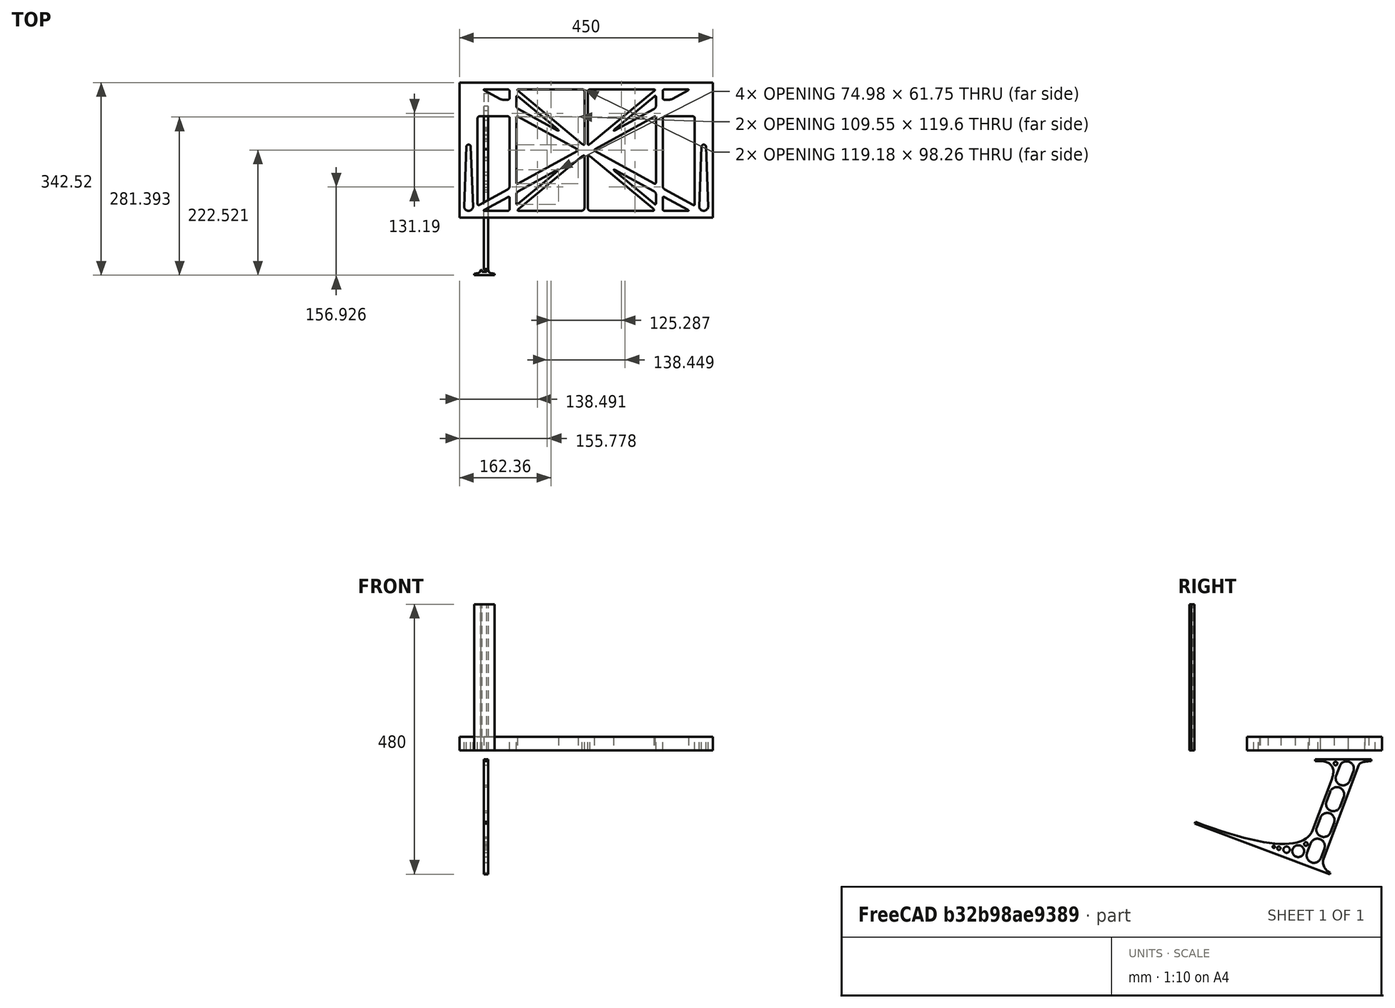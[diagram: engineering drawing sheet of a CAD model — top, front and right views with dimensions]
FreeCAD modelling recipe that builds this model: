
FCSTD DOCUMENT  (FreeCAD 0.19R0.19.2)
Label: laptopStand170FCStd
License: All rights reserved
LicenseURL: http://en.wikipedia.org/wiki/All_rights_reserved
objects: Sketcher::SketchObject×4, Part::Extrusion×3
note: 7 computed .brp shape members not serialized (recipe doc carries the construction recipe); baked Part::Feature solids carry a one-line shape summary decoded from their .brp

FEATURE [Sketcher::SketchObject] Sketch
  FullyConstrained = false
  sketch-geometry (349):
    g0: LineSegment StartX=-10.9272 StartY=-82.7794 StartZ=0 EndX=46.0728 EndY=-51.4823 EndZ=0
    g1: LineSegment StartX=-10.9272 StartY=76.4095 StartZ=0 EndX=-10.9272 EndY=-82.7794 EndZ=0
    g2: LineSegment StartX=46.0728 StartY=76.4095 StartZ=0 EndX=46.0728 EndY=-51.4823 EndZ=0
    g3: LineSegment StartX=-42.9272 StartY=136.221 StartZ=0 EndX=-42.9272 EndY=-103.779 EndZ=0
    g4: LineSegment StartX=407.073 StartY=136.221 StartZ=0 EndX=407.073 EndY=-103.779 EndZ=0
    g5: ArcOfCircle CenterX=-26.9272 CenterY=-83.7794 CenterZ=0 NormalX=0 NormalY=0 NormalZ=1 AngleXU=0 Radius=8 StartAngle=3.14159 EndAngle=6.28319
    g6: ArcOfCircle CenterX=391.073 CenterY=22.1087 CenterZ=0 NormalX=0 NormalY=0 NormalZ=1 AngleXU=0 Radius=8 StartAngle=-4.4e-15 EndAngle=3.14159
    g7: LineSegment StartX=399.073 StartY=22.1087 StartZ=0 EndX=399.073 EndY=-83.7794 EndZ=0
    g8: LineSegment StartX=383.073 StartY=22.1087 StartZ=0 EndX=383.073 EndY=-83.7794 EndZ=0
    g9: ArcOfCircle CenterX=391.073 CenterY=-83.7794 CenterZ=0 NormalX=0 NormalY=0 NormalZ=1 AngleXU=0 Radius=8 StartAngle=3.14159 EndAngle=6.28319
    g10: Circle CenterX=175.022 CenterY=27.0628 CenterZ=0 NormalX=0 NormalY=0 NormalZ=1 AngleXU=0 Radius=1
    g11: Circle CenterX=179.022 CenterY=24.8665 CenterZ=0 NormalX=0 NormalY=0 NormalZ=1 AngleXU=0 Radius=1
    g12: Circle CenterX=179.022 CenterY=27.0628 CenterZ=0 NormalX=0 NormalY=0 NormalZ=1 AngleXU=0 Radius=1
    g13: BSplineCurve PolesCount=3 KnotsCount=2 Degree=2 IsPeriodic=0
    g14: GeomPoint X=175.022 Y=27.0628 Z=0
    g15: GeomPoint X=179.022 Y=27.0628 Z=0
    g16: Circle CenterX=189.124 CenterY=27.0628 CenterZ=0 NormalX=0 NormalY=0 NormalZ=1 AngleXU=0 Radius=1
    g17: Circle CenterX=185.124 CenterY=24.8665 CenterZ=0 NormalX=0 NormalY=0 NormalZ=1 AngleXU=0 Radius=1
    g18: Circle CenterX=185.124 CenterY=27.0628 CenterZ=0 NormalX=0 NormalY=0 NormalZ=1 AngleXU=0 Radius=1
    g19: BSplineCurve PolesCount=3 KnotsCount=2 Degree=2 IsPeriodic=0
    g20: GeomPoint X=189.124 Y=27.0628 Z=0
    g21: GeomPoint X=185.124 Y=27.0628 Z=0
    g22: Circle CenterX=175.022 CenterY=5.37834 CenterZ=0 NormalX=0 NormalY=0 NormalZ=1 AngleXU=0 Radius=1
    g23: Circle CenterX=179.022 CenterY=7.57463 CenterZ=0 NormalX=0 NormalY=0 NormalZ=1 AngleXU=0 Radius=1
    g24: Circle CenterX=179.022 CenterY=5.34704 CenterZ=0 NormalX=0 NormalY=0 NormalZ=1 AngleXU=0 Radius=1
    g25: BSplineCurve PolesCount=3 KnotsCount=2 Degree=2 IsPeriodic=0
    g26: GeomPoint X=175.022 Y=5.37834 Z=0
    g27: GeomPoint X=179.022 Y=5.34704 Z=0
    g28: Circle CenterX=189.124 CenterY=5.37834 CenterZ=0 NormalX=0 NormalY=0 NormalZ=1 AngleXU=0 Radius=1
    g29: Circle CenterX=185.124 CenterY=7.57463 CenterZ=0 NormalX=0 NormalY=0 NormalZ=1 AngleXU=0 Radius=1
    g30: Circle CenterX=185.124 CenterY=5.34704 CenterZ=0 NormalX=0 NormalY=0 NormalZ=1 AngleXU=0 Radius=1
    g31: BSplineCurve PolesCount=3 KnotsCount=2 Degree=2 IsPeriodic=0
    g32: GeomPoint X=189.124 Y=5.37834 Z=0
    g33: GeomPoint X=185.124 Y=5.34704 Z=0
    g34: Circle CenterX=165.871 CenterY=18.1458 CenterZ=0 NormalX=0 NormalY=0 NormalZ=1 AngleXU=0 Radius=1
    g35: Circle CenterX=169.377 CenterY=16.2206 CenterZ=0 NormalX=0 NormalY=0 NormalZ=1 AngleXU=0 Radius=1
    g36: Circle CenterX=165.871 CenterY=14.2954 CenterZ=0 NormalX=0 NormalY=0 NormalZ=1 AngleXU=0 Radius=1
    g37: BSplineCurve PolesCount=3 KnotsCount=2 Degree=2 IsPeriodic=0
    g38: GeomPoint X=165.871 Y=18.1458 Z=0
    g39: GeomPoint X=165.871 Y=14.2954 Z=0
    g40: Circle CenterX=198.275 CenterY=18.1458 CenterZ=0 NormalX=0 NormalY=0 NormalZ=1 AngleXU=0 Radius=1
    g41: Circle CenterX=194.768 CenterY=16.2206 CenterZ=0 NormalX=0 NormalY=0 NormalZ=1 AngleXU=0 Radius=1
    g42: Circle CenterX=198.275 CenterY=14.2954 CenterZ=0 NormalX=0 NormalY=0 NormalZ=1 AngleXU=0 Radius=1
    g43: BSplineCurve PolesCount=3 KnotsCount=2 Degree=2 IsPeriodic=0
    g44: GeomPoint X=198.275 Y=18.1458 Z=0
    g45: GeomPoint X=198.275 Y=14.2954 Z=0
    g46: LineSegment StartX=407.073 StartY=-103.779 StartZ=0 EndX=-42.9272 EndY=-103.779 EndZ=0
    g47: LineSegment StartX=407.073 StartY=136.221 StartZ=0 EndX=-42.9272 EndY=136.221 EndZ=0
    g48: LineSegment StartX=46.0728 StartY=76.4095 StartZ=0 EndX=-10.9272 EndY=76.4095 EndZ=0
    g49: Circle CenterX=125.607 CenterY=54.1951 CenterZ=0 NormalX=0 NormalY=0 NormalZ=1 AngleXU=0 Radius=1
    g50: Circle CenterX=139.632 CenterY=46.4944 CenterZ=0 NormalX=0 NormalY=0 NormalZ=1 AngleXU=0 Radius=1
    g51: Circle CenterX=127.326 CenterY=56.7187 CenterZ=0 NormalX=0 NormalY=0 NormalZ=1 AngleXU=0 Radius=1
    g52: BSplineCurve PolesCount=3 KnotsCount=2 Degree=2 IsPeriodic=0
    g53: GeomPoint X=125.607 Y=54.1951 Z=0
    g54: GeomPoint X=127.326 Y=56.7187 Z=0
    g55: Circle CenterX=236.821 CenterY=56.7187 CenterZ=0 NormalX=0 NormalY=0 NormalZ=1 AngleXU=0 Radius=1
    g56: Circle CenterX=224.513 CenterY=46.4944 CenterZ=0 NormalX=0 NormalY=0 NormalZ=1 AngleXU=0 Radius=1
    g57: Circle CenterX=238.538 CenterY=54.1951 CenterZ=0 NormalX=0 NormalY=0 NormalZ=1 AngleXU=0 Radius=1
    g58: BSplineCurve PolesCount=3 KnotsCount=2 Degree=2 IsPeriodic=0
    g59: GeomPoint X=236.821 Y=56.7187 Z=0
    g60: GeomPoint X=238.538 Y=54.1951 Z=0
    g61: Circle CenterX=238.538 CenterY=-21.7539 CenterZ=0 NormalX=0 NormalY=0 NormalZ=1 AngleXU=0 Radius=1
    g62: Circle CenterX=224.513 CenterY=-14.0532 CenterZ=0 NormalX=0 NormalY=0 NormalZ=1 AngleXU=0 Radius=1
    g63: Circle CenterX=236.821 CenterY=-24.2775 CenterZ=0 NormalX=0 NormalY=0 NormalZ=1 AngleXU=0 Radius=1
    g64: BSplineCurve PolesCount=3 KnotsCount=2 Degree=2 IsPeriodic=0
    g65: GeomPoint X=238.538 Y=-21.7539 Z=0
    g66: GeomPoint X=236.821 Y=-24.2775 Z=0
    g67: Circle CenterX=125.607 CenterY=-21.7539 CenterZ=0 NormalX=0 NormalY=0 NormalZ=1 AngleXU=0 Radius=1
    g68: Circle CenterX=139.632 CenterY=-14.0532 CenterZ=0 NormalX=0 NormalY=0 NormalZ=1 AngleXU=0 Radius=1
    g69: Circle CenterX=127.325 CenterY=-24.2775 CenterZ=0 NormalX=0 NormalY=0 NormalZ=1 AngleXU=0 Radius=1
    g70: BSplineCurve PolesCount=3 KnotsCount=2 Degree=2 IsPeriodic=0
    g71: GeomPoint X=125.607 Y=-21.7539 Z=0
    g72: GeomPoint X=127.325 Y=-24.2775 Z=0
    g73: Circle CenterX=302.996 CenterY=111.695 CenterZ=0 NormalX=0 NormalY=0 NormalZ=1 AngleXU=0 Radius=1
    g74: Circle CenterX=306.073 CenterY=114.251 CenterZ=0 NormalX=0 NormalY=0 NormalZ=1 AngleXU=0 Radius=1
    g75: Circle CenterX=306.073 CenterY=110.251 CenterZ=0 NormalX=0 NormalY=0 NormalZ=1 AngleXU=0 Radius=1
    g76: BSplineCurve PolesCount=3 KnotsCount=2 Degree=2 IsPeriodic=0
    g77: GeomPoint X=302.996 Y=111.695 Z=0
    g78: GeomPoint X=306.073 Y=110.251 Z=0
    g79: Circle CenterX=306.073 CenterY=95.2763 CenterZ=0 NormalX=0 NormalY=0 NormalZ=1 AngleXU=0 Radius=1
    g80: Circle CenterX=306.073 CenterY=91.2763 CenterZ=0 NormalX=0 NormalY=0 NormalZ=1 AngleXU=0 Radius=1
    g81: Circle CenterX=302.567 CenterY=89.3511 CenterZ=0 NormalX=0 NormalY=0 NormalZ=1 AngleXU=0 Radius=1
    g82: BSplineCurve PolesCount=3 KnotsCount=2 Degree=2 IsPeriodic=0
    g83: GeomPoint X=306.073 Y=95.2763 Z=0
    g84: GeomPoint X=302.567 Y=89.3511 Z=0
    g85: LineSegment StartX=306.073 StartY=110.251 StartZ=0 EndX=306.073 EndY=95.2763 EndZ=0
    g86: LineSegment StartX=302.996 StartY=111.695 StartZ=0 EndX=236.821 EndY=56.7187 EndZ=0
    g87: LineSegment StartX=238.538 StartY=54.1951 StartZ=0 EndX=302.567 EndY=89.3511 EndZ=0
    g88: Circle CenterX=61.1496 CenterY=111.695 CenterZ=0 NormalX=0 NormalY=0 NormalZ=1 AngleXU=0 Radius=1
    g89: Circle CenterX=58.0728 CenterY=114.251 CenterZ=0 NormalX=0 NormalY=0 NormalZ=1 AngleXU=0 Radius=1
    g90: Circle CenterX=58.0728 CenterY=110.251 CenterZ=0 NormalX=0 NormalY=0 NormalZ=1 AngleXU=0 Radius=1
    g91: BSplineCurve PolesCount=3 KnotsCount=2 Degree=2 IsPeriodic=0
    g92: GeomPoint X=61.1496 Y=111.695 Z=0
    g93: GeomPoint X=58.0728 Y=110.251 Z=0
    g94: Circle CenterX=61.5791 CenterY=89.3511 CenterZ=0 NormalX=0 NormalY=0 NormalZ=1 AngleXU=0 Radius=1
    g95: Circle CenterX=58.0728 CenterY=91.2763 CenterZ=0 NormalX=0 NormalY=0 NormalZ=1 AngleXU=0 Radius=1
    g96: Circle CenterX=58.0728 CenterY=95.2763 CenterZ=0 NormalX=0 NormalY=0 NormalZ=1 AngleXU=0 Radius=1
    g97: BSplineCurve PolesCount=3 KnotsCount=2 Degree=2 IsPeriodic=0
    g98: GeomPoint X=61.5791 Y=89.3511 Z=0
    g99: GeomPoint X=58.0728 Y=95.2763 Z=0
    g100: LineSegment StartX=58.0728 StartY=110.251 StartZ=0 EndX=58.0728 EndY=95.2763 EndZ=0
    g101: LineSegment StartX=61.1496 StartY=111.695 StartZ=0 EndX=127.326 EndY=56.7187 EndZ=0
    g102: LineSegment StartX=125.607 StartY=54.1951 StartZ=0 EndX=61.5791 EndY=89.3511 EndZ=0
    g103: Circle CenterX=61.5791 CenterY=-56.9099 CenterZ=0 NormalX=0 NormalY=0 NormalZ=1 AngleXU=0 Radius=1
    g104: Circle CenterX=58.0728 CenterY=-58.8351 CenterZ=0 NormalX=0 NormalY=0 NormalZ=1 AngleXU=0 Radius=1
    g105: Circle CenterX=58.0728 CenterY=-62.8351 CenterZ=0 NormalX=0 NormalY=0 NormalZ=1 AngleXU=0 Radius=1
    g106: BSplineCurve PolesCount=3 KnotsCount=2 Degree=2 IsPeriodic=0
    g107: GeomPoint X=61.5791 Y=-56.9099 Z=0
    g108: GeomPoint X=58.0728 Y=-62.8351 Z=0
    g109: Circle CenterX=58.0728 CenterY=-77.8102 CenterZ=0 NormalX=0 NormalY=0 NormalZ=1 AngleXU=0 Radius=1
    g110: Circle CenterX=58.0728 CenterY=-81.8102 CenterZ=0 NormalX=0 NormalY=0 NormalZ=1 AngleXU=0 Radius=1
    g111: Circle CenterX=61.1496 CenterY=-79.2541 CenterZ=0 NormalX=0 NormalY=0 NormalZ=1 AngleXU=0 Radius=1
    g112: BSplineCurve PolesCount=3 KnotsCount=2 Degree=2 IsPeriodic=0
    g113: GeomPoint X=58.0728 Y=-77.8102 Z=0
    g114: GeomPoint X=61.1496 Y=-79.2541 Z=0
    g115: LineSegment StartX=58.0728 StartY=-62.8351 StartZ=0 EndX=58.0728 EndY=-77.8102 EndZ=0
    g116: LineSegment StartX=61.1496 StartY=-79.2541 StartZ=0 EndX=127.325 EndY=-24.2775 EndZ=0
    g117: LineSegment StartX=125.607 StartY=-21.7539 StartZ=0 EndX=61.5791 EndY=-56.9099 EndZ=0
    g118: Circle CenterX=302.567 CenterY=-56.9099 CenterZ=0 NormalX=0 NormalY=0 NormalZ=1 AngleXU=0 Radius=1
    g119: Circle CenterX=306.073 CenterY=-58.8351 CenterZ=0 NormalX=0 NormalY=0 NormalZ=1 AngleXU=0 Radius=1
    g120: Circle CenterX=306.073 CenterY=-62.8351 CenterZ=0 NormalX=0 NormalY=0 NormalZ=1 AngleXU=0 Radius=1
    g121: BSplineCurve PolesCount=3 KnotsCount=2 Degree=2 IsPeriodic=0
    g122: GeomPoint X=302.567 Y=-56.9099 Z=0
    g123: GeomPoint X=306.073 Y=-62.8351 Z=0
    g124: Circle CenterX=302.996 CenterY=-79.2541 CenterZ=0 NormalX=0 NormalY=0 NormalZ=1 AngleXU=0 Radius=1
    g125: Circle CenterX=306.073 CenterY=-81.8102 CenterZ=0 NormalX=0 NormalY=0 NormalZ=1 AngleXU=0 Radius=1
    g126: Circle CenterX=306.073 CenterY=-77.8102 CenterZ=0 NormalX=0 NormalY=0 NormalZ=1 AngleXU=0 Radius=1
    g127: BSplineCurve PolesCount=3 KnotsCount=2 Degree=2 IsPeriodic=0
    g128: GeomPoint X=302.996 Y=-79.2541 Z=0
    g129: GeomPoint X=306.073 Y=-77.8102 Z=0
    g130: LineSegment StartX=306.073 StartY=-62.8351 StartZ=0 EndX=306.073 EndY=-77.8102 EndZ=0
    g131: LineSegment StartX=302.996 StartY=-79.2541 StartZ=0 EndX=236.821 EndY=-24.2775 EndZ=0
    g132: LineSegment StartX=238.538 StartY=-21.7539 StartZ=0 EndX=302.567 EndY=-56.9099 EndZ=0
    g133: Circle CenterX=61.6457 CenterY=-88.8112 CenterZ=0 NormalX=0 NormalY=0 NormalZ=1 AngleXU=0 Radius=1
    g134: Circle CenterX=58.0728 CenterY=-91.7794 CenterZ=0 NormalX=0 NormalY=0 NormalZ=1 AngleXU=0 Radius=1
    g135: Circle CenterX=63.9135 CenterY=-91.7794 CenterZ=0 NormalX=0 NormalY=0 NormalZ=1 AngleXU=0 Radius=1
    g136: BSplineCurve PolesCount=3 KnotsCount=2 Degree=2 IsPeriodic=0
    g137: GeomPoint X=61.6457 Y=-88.8112 Z=0
    g138: GeomPoint X=63.9135 Y=-91.7794 Z=0
    g139: Circle CenterX=179.022 CenterY=-85.8163 CenterZ=0 NormalX=0 NormalY=0 NormalZ=1 AngleXU=0 Radius=1
    g140: Circle CenterX=179.022 CenterY=-91.7794 CenterZ=0 NormalX=0 NormalY=0 NormalZ=1 AngleXU=0 Radius=1
    g141: Circle CenterX=171.895 CenterY=-91.7794 CenterZ=0 NormalX=0 NormalY=0 NormalZ=1 AngleXU=0 Radius=1
    g142: BSplineCurve PolesCount=3 KnotsCount=2 Degree=2 IsPeriodic=0
    g143: GeomPoint X=179.022 Y=-85.8163 Z=0
    g144: GeomPoint X=171.895 Y=-91.7794 Z=0
    g145: Circle CenterX=185.124 CenterY=-86.2028 CenterZ=0 NormalX=0 NormalY=0 NormalZ=1 AngleXU=0 Radius=1
    g146: Circle CenterX=185.124 CenterY=-91.7794 CenterZ=0 NormalX=0 NormalY=0 NormalZ=1 AngleXU=0 Radius=1
    g147: Circle CenterX=191.747 CenterY=-91.7794 CenterZ=0 NormalX=0 NormalY=0 NormalZ=1 AngleXU=0 Radius=1
    g148: BSplineCurve PolesCount=3 KnotsCount=2 Degree=2 IsPeriodic=0
    g149: GeomPoint X=185.124 Y=-86.2028 Z=0
    g150: GeomPoint X=191.747 Y=-91.7794 Z=0
    g151: Circle CenterX=299.888 CenterY=-86.6413 CenterZ=0 NormalX=0 NormalY=0 NormalZ=1 AngleXU=0 Radius=1
    g152: Circle CenterX=306.073 CenterY=-91.7794 CenterZ=0 NormalX=0 NormalY=0 NormalZ=1 AngleXU=0 Radius=1
    g153: Circle CenterX=298.776 CenterY=-91.7794 CenterZ=0 NormalX=0 NormalY=0 NormalZ=1 AngleXU=0 Radius=1
    g154: BSplineCurve PolesCount=3 KnotsCount=2 Degree=2 IsPeriodic=0
    g155: GeomPoint X=299.888 Y=-86.6413 Z=0
    g156: GeomPoint X=298.776 Y=-91.7794 Z=0
    g157: LineSegment StartX=189.124 StartY=5.37834 StartZ=0 EndX=299.888 EndY=-86.6413 EndZ=0
    g158: LineSegment StartX=298.776 StartY=-91.7794 StartZ=0 EndX=191.747 EndY=-91.7794 EndZ=0
    g159: LineSegment StartX=185.124 StartY=-86.2028 StartZ=0 EndX=185.124 EndY=5.34704 EndZ=0
    g160: LineSegment StartX=179.022 StartY=5.34704 StartZ=0 EndX=179.022 EndY=-85.8163 EndZ=0
    g161: LineSegment StartX=171.895 StartY=-91.7794 StartZ=0 EndX=63.9135 EndY=-91.7794 EndZ=0
    g162: LineSegment StartX=61.6457 StartY=-88.8112 StartZ=0 EndX=175.022 EndY=5.37834 EndZ=0
    g163: Circle CenterX=302.073 CenterY=124.221 CenterZ=0 NormalX=0 NormalY=0 NormalZ=1 AngleXU=0 Radius=1
    g164: Circle CenterX=306.073 CenterY=124.221 CenterZ=0 NormalX=0 NormalY=0 NormalZ=1 AngleXU=0 Radius=1
    g165: Circle CenterX=302.996 CenterY=121.665 CenterZ=0 NormalX=0 NormalY=0 NormalZ=1 AngleXU=0 Radius=1
    g166: BSplineCurve PolesCount=3 KnotsCount=2 Degree=2 IsPeriodic=0
    g167: GeomPoint X=302.073 Y=124.221 Z=0
    g168: GeomPoint X=302.996 Y=121.665 Z=0
    g169: Circle CenterX=189.124 CenterY=124.221 CenterZ=0 NormalX=0 NormalY=0 NormalZ=1 AngleXU=0 Radius=1
    g170: Circle CenterX=185.124 CenterY=124.221 CenterZ=0 NormalX=0 NormalY=0 NormalZ=1 AngleXU=0 Radius=1
    g171: Circle CenterX=185.124 CenterY=120.221 CenterZ=0 NormalX=0 NormalY=0 NormalZ=1 AngleXU=0 Radius=1
    g172: BSplineCurve PolesCount=3 KnotsCount=2 Degree=2 IsPeriodic=0
    g173: GeomPoint X=189.124 Y=124.221 Z=0
    g174: GeomPoint X=185.124 Y=120.221 Z=0
    g175: Circle CenterX=175.022 CenterY=124.221 CenterZ=0 NormalX=0 NormalY=0 NormalZ=1 AngleXU=0 Radius=1
    g176: Circle CenterX=179.022 CenterY=124.221 CenterZ=0 NormalX=0 NormalY=0 NormalZ=1 AngleXU=0 Radius=1
    g177: Circle CenterX=179.022 CenterY=120.221 CenterZ=0 NormalX=0 NormalY=0 NormalZ=1 AngleXU=0 Radius=1
    g178: BSplineCurve PolesCount=3 KnotsCount=2 Degree=2 IsPeriodic=0
    g179: GeomPoint X=175.022 Y=124.221 Z=0
    g180: GeomPoint X=179.022 Y=120.221 Z=0
    g181: Circle CenterX=62.0728 CenterY=124.221 CenterZ=0 NormalX=0 NormalY=0 NormalZ=1 AngleXU=0 Radius=1
    g182: Circle CenterX=58.0728 CenterY=124.221 CenterZ=0 NormalX=0 NormalY=0 NormalZ=1 AngleXU=0 Radius=1
    g183: Circle CenterX=61.1496 CenterY=121.665 CenterZ=0 NormalX=0 NormalY=0 NormalZ=1 AngleXU=0 Radius=1
    g184: BSplineCurve PolesCount=3 KnotsCount=2 Degree=2 IsPeriodic=0
    g185: GeomPoint X=62.0728 Y=124.221 Z=0
    g186: GeomPoint X=61.1496 Y=121.665 Z=0
    g187: LineSegment StartX=62.0728 StartY=124.221 StartZ=0 EndX=175.022 EndY=124.221 EndZ=0
    g188: LineSegment StartX=179.022 StartY=120.221 StartZ=0 EndX=179.022 EndY=27.0628 EndZ=0
    g189: LineSegment StartX=185.124 StartY=27.0628 StartZ=0 EndX=185.124 EndY=120.221 EndZ=0
    g190: LineSegment StartX=189.124 StartY=124.221 StartZ=0 EndX=302.073 EndY=124.221 EndZ=0
    g191: LineSegment StartX=302.996 StartY=121.665 StartZ=0 EndX=189.124 EndY=27.0628 EndZ=0
    g192: LineSegment StartX=175.022 StartY=27.0628 StartZ=0 EndX=61.1496 EndY=121.665 EndZ=0
    g193: Circle CenterX=61.5791 CenterY=75.4095 CenterZ=0 NormalX=0 NormalY=0 NormalZ=1 AngleXU=0 Radius=1
    g194: Circle CenterX=58.0728 CenterY=77.3346 CenterZ=0 NormalX=0 NormalY=0 NormalZ=1 AngleXU=0 Radius=1
    g195: Circle CenterX=58.0728 CenterY=73.3346 CenterZ=0 NormalX=0 NormalY=0 NormalZ=1 AngleXU=0 Radius=1
    g196: BSplineCurve PolesCount=3 KnotsCount=2 Degree=2 IsPeriodic=0
    g197: GeomPoint X=61.5791 Y=75.4095 Z=0
    g198: GeomPoint X=58.0728 Y=73.3346 Z=0
    g199: Circle CenterX=58.0728 CenterY=-40.8935 CenterZ=0 NormalX=0 NormalY=0 NormalZ=1 AngleXU=0 Radius=1
    g200: Circle CenterX=58.0728 CenterY=-44.8935 CenterZ=0 NormalX=0 NormalY=0 NormalZ=1 AngleXU=0 Radius=1
    g201: Circle CenterX=61.5791 CenterY=-42.9683 CenterZ=0 NormalX=0 NormalY=0 NormalZ=1 AngleXU=0 Radius=1
    g202: BSplineCurve PolesCount=3 KnotsCount=2 Degree=2 IsPeriodic=0
    g203: GeomPoint X=58.0728 Y=-40.8935 Z=0
    g204: GeomPoint X=61.5791 Y=-42.9683 Z=0
    g205: LineSegment StartX=61.5791 StartY=-42.9683 StartZ=0 EndX=165.871 EndY=14.2954 EndZ=0
    g206: LineSegment StartX=165.871 StartY=18.1458 StartZ=0 EndX=61.5791 EndY=75.4095 EndZ=0
    g207: LineSegment StartX=58.0728 StartY=73.3346 StartZ=0 EndX=58.0728 EndY=-40.8935 EndZ=0
    g208: Circle CenterX=302.567 CenterY=-42.9683 CenterZ=0 NormalX=0 NormalY=0 NormalZ=1 AngleXU=0 Radius=1
    g209: Circle CenterX=306.073 CenterY=-44.8935 CenterZ=0 NormalX=0 NormalY=0 NormalZ=1 AngleXU=0 Radius=1
    g210: Circle CenterX=306.073 CenterY=-40.8935 CenterZ=0 NormalX=0 NormalY=0 NormalZ=1 AngleXU=0 Radius=1
    g211: BSplineCurve PolesCount=3 KnotsCount=2 Degree=2 IsPeriodic=0
    g212: GeomPoint X=302.567 Y=-42.9683 Z=0
    g213: GeomPoint X=306.073 Y=-40.8935 Z=0
    g214: Circle CenterX=306.073 CenterY=73.3346 CenterZ=0 NormalX=0 NormalY=0 NormalZ=1 AngleXU=0 Radius=1
    g215: Circle CenterX=306.073 CenterY=77.3346 CenterZ=0 NormalX=0 NormalY=0 NormalZ=1 AngleXU=0 Radius=1
    g216: Circle CenterX=302.567 CenterY=75.4095 CenterZ=0 NormalX=0 NormalY=0 NormalZ=1 AngleXU=0 Radius=1
    g217: BSplineCurve PolesCount=3 KnotsCount=2 Degree=2 IsPeriodic=0
    g218: GeomPoint X=306.073 Y=73.3346 Z=0
    g219: GeomPoint X=302.567 Y=75.4095 Z=0
    g220: LineSegment StartX=302.567 StartY=-42.9683 StartZ=0 EndX=198.275 EndY=14.2954 EndZ=0
    g221: LineSegment StartX=198.275 StartY=18.1458 StartZ=0 EndX=302.567 EndY=75.4095 EndZ=0
    g222: LineSegment StartX=306.073 StartY=73.3346 StartZ=0 EndX=306.073 EndY=-40.8935 EndZ=0
    g223: LineSegment StartX=322.073 StartY=105.865 StartZ=0 EndX=328.643 EndY=105.865 EndZ=0
    g224: LineSegment StartX=318.073 StartY=120.221 StartZ=0 EndX=318.073 EndY=109.865 EndZ=0
    g225: LineSegment StartX=336.157 StartY=107.779 StartZ=0 EndX=362.567 EndY=122.294 EndZ=0
    g226: Circle CenterX=362.073 CenterY=124.221 CenterZ=0 NormalX=0 NormalY=0 NormalZ=1 AngleXU=0 Radius=1
    g227: Circle CenterX=366.073 CenterY=124.221 CenterZ=0 NormalX=0 NormalY=0 NormalZ=1 AngleXU=0 Radius=1
    g228: Circle CenterX=362.567 CenterY=122.294 CenterZ=0 NormalX=0 NormalY=0 NormalZ=1 AngleXU=0 Radius=1
    g229: BSplineCurve PolesCount=3 KnotsCount=2 Degree=2 IsPeriodic=0
    g230: GeomPoint X=362.073 Y=124.221 Z=0
    g231: GeomPoint X=362.567 Y=122.294 Z=0
    g232: Circle CenterX=322.073 CenterY=124.221 CenterZ=0 NormalX=0 NormalY=0 NormalZ=1 AngleXU=0 Radius=1
    g233: Circle CenterX=318.073 CenterY=124.221 CenterZ=0 NormalX=0 NormalY=0 NormalZ=1 AngleXU=0 Radius=1
    g234: Circle CenterX=318.073 CenterY=120.221 CenterZ=0 NormalX=0 NormalY=0 NormalZ=1 AngleXU=0 Radius=1
    g235: BSplineCurve PolesCount=3 KnotsCount=2 Degree=2 IsPeriodic=0
    g236: GeomPoint X=322.073 Y=124.221 Z=0
    g237: GeomPoint X=318.073 Y=120.221 Z=0
    g238: Circle CenterX=322.073 CenterY=105.865 CenterZ=0 NormalX=0 NormalY=0 NormalZ=1 AngleXU=0 Radius=1
    g239: Circle CenterX=318.073 CenterY=105.865 CenterZ=0 NormalX=0 NormalY=0 NormalZ=1 AngleXU=0 Radius=1
    g240: Circle CenterX=318.073 CenterY=109.865 CenterZ=0 NormalX=0 NormalY=0 NormalZ=1 AngleXU=0 Radius=1
    g241: BSplineCurve PolesCount=3 KnotsCount=2 Degree=2 IsPeriodic=0
    g242: GeomPoint X=322.073 Y=105.865 Z=0
    g243: GeomPoint X=318.073 Y=109.865 Z=0
    g244: Circle CenterX=336.157 CenterY=107.779 CenterZ=0 NormalX=0 NormalY=0 NormalZ=1 AngleXU=0 Radius=1
    g245: Circle CenterX=332.651 CenterY=105.853 CenterZ=0 NormalX=0 NormalY=0 NormalZ=1 AngleXU=0 Radius=1
    g246: Circle CenterX=328.643 CenterY=105.865 CenterZ=0 NormalX=0 NormalY=0 NormalZ=1 AngleXU=0 Radius=1
    g247: BSplineCurve PolesCount=3 KnotsCount=2 Degree=2 IsPeriodic=0
    g248: GeomPoint X=336.157 Y=107.779 Z=0
    g249: GeomPoint X=328.643 Y=105.865 Z=0
    g250: LineSegment StartX=322.073 StartY=124.221 StartZ=0 EndX=362.073 EndY=124.221 EndZ=0
    g251: Circle CenterX=371.567 CenterY=-80.8644 CenterZ=0 NormalX=0 NormalY=0 NormalZ=1 AngleXU=0 Radius=1
    g252: Circle CenterX=375.073 CenterY=-82.7896 CenterZ=0 NormalX=0 NormalY=0 NormalZ=1 AngleXU=0 Radius=1
    g253: Circle CenterX=375.073 CenterY=-78.7896 CenterZ=0 NormalX=0 NormalY=0 NormalZ=1 AngleXU=0 Radius=1
    g254: BSplineCurve PolesCount=3 KnotsCount=2 Degree=2 IsPeriodic=0
    g255: GeomPoint X=371.567 Y=-80.8644 Z=0
    g256: GeomPoint X=375.073 Y=-78.7896 Z=0
    g257: Circle CenterX=321.579 CenterY=-53.4075 CenterZ=0 NormalX=0 NormalY=0 NormalZ=1 AngleXU=0 Radius=1
    g258: Circle CenterX=318.073 CenterY=-51.4823 CenterZ=0 NormalX=0 NormalY=0 NormalZ=1 AngleXU=0 Radius=1
    g259: Circle CenterX=318.073 CenterY=-47.4805 CenterZ=0 NormalX=0 NormalY=0 NormalZ=1 AngleXU=0 Radius=1
    g260: BSplineCurve PolesCount=3 KnotsCount=2 Degree=2 IsPeriodic=0
    g261: GeomPoint X=321.579 Y=-53.4075 Z=0
    g262: GeomPoint X=318.073 Y=-47.4805 Z=0
    g263: LineSegment StartX=371.567 StartY=-80.8644 StartZ=0 EndX=321.579 EndY=-53.4075 EndZ=0
    g264: Circle CenterX=321.579 CenterY=-67.3492 CenterZ=0 NormalX=0 NormalY=0 NormalZ=1 AngleXU=0 Radius=1
    g265: Circle CenterX=318.073 CenterY=-65.424 CenterZ=0 NormalX=0 NormalY=0 NormalZ=1 AngleXU=0 Radius=1
    g266: Circle CenterX=318.073 CenterY=-69.424 CenterZ=0 NormalX=0 NormalY=0 NormalZ=1 AngleXU=0 Radius=1
    g267: BSplineCurve PolesCount=3 KnotsCount=2 Degree=2 IsPeriodic=0
    g268: GeomPoint X=321.579 Y=-67.3492 Z=0
    g269: GeomPoint X=318.073 Y=-69.424 Z=0
    g270: Circle CenterX=362.567 CenterY=-89.8542 CenterZ=0 NormalX=0 NormalY=0 NormalZ=1 AngleXU=0 Radius=1
    g271: Circle CenterX=366.073 CenterY=-91.7794 CenterZ=0 NormalX=0 NormalY=0 NormalZ=1 AngleXU=0 Radius=1
    g272: Circle CenterX=362.073 CenterY=-91.7794 CenterZ=0 NormalX=0 NormalY=0 NormalZ=1 AngleXU=0 Radius=1
    g273: BSplineCurve PolesCount=3 KnotsCount=2 Degree=2 IsPeriodic=0
    g274: GeomPoint X=362.567 Y=-89.8542 Z=0
    g275: GeomPoint X=362.073 Y=-91.7794 Z=0
    g276: Circle CenterX=322.073 CenterY=-91.7794 CenterZ=0 NormalX=0 NormalY=0 NormalZ=1 AngleXU=0 Radius=1
    g277: Circle CenterX=318.073 CenterY=-91.7794 CenterZ=0 NormalX=0 NormalY=0 NormalZ=1 AngleXU=0 Radius=1
    g278: Circle CenterX=318.073 CenterY=-87.7794 CenterZ=0 NormalX=0 NormalY=0 NormalZ=1 AngleXU=0 Radius=1
    g279: BSplineCurve PolesCount=3 KnotsCount=2 Degree=2 IsPeriodic=0
    g280: GeomPoint X=322.073 Y=-91.7794 Z=0
    g281: GeomPoint X=318.073 Y=-87.7794 Z=0
    g282: LineSegment StartX=362.567 StartY=-89.8542 StartZ=0 EndX=321.579 EndY=-67.3492 EndZ=0
    g283: LineSegment StartX=318.073 StartY=-69.424 StartZ=0 EndX=318.073 EndY=-87.7794 EndZ=0
    g284: LineSegment StartX=322.073 StartY=-91.7794 StartZ=0 EndX=362.073 EndY=-91.7794 EndZ=0
    g285: Circle CenterX=2.07281 CenterY=124.221 CenterZ=0 NormalX=0 NormalY=0 NormalZ=1 AngleXU=0 Radius=1
    g286: Circle CenterX=1.57905 CenterY=122.295 CenterZ=0 NormalX=0 NormalY=0 NormalZ=1 AngleXU=0 Radius=1
    g287: BSplineCurve PolesCount=3 KnotsCount=2 Degree=2 IsPeriodic=0
    g288: GeomPoint X=2.07281 Y=124.221 Z=0
    g289: GeomPoint X=1.57905 Y=122.295 Z=0
    g290: Circle CenterX=42.0728 CenterY=124.221 CenterZ=0 NormalX=0 NormalY=0 NormalZ=1 AngleXU=0 Radius=1
    g291: Circle CenterX=46.0728 CenterY=124.221 CenterZ=0 NormalX=0 NormalY=0 NormalZ=1 AngleXU=0 Radius=1
    g292: Circle CenterX=46.0728 CenterY=120.221 CenterZ=0 NormalX=0 NormalY=0 NormalZ=1 AngleXU=0 Radius=1
    g293: BSplineCurve PolesCount=3 KnotsCount=2 Degree=2 IsPeriodic=0
    g294: GeomPoint X=42.0728 Y=124.221 Z=0
    g295: GeomPoint X=46.0728 Y=120.221 Z=0
    g296: Circle CenterX=46.0728 CenterY=109.865 CenterZ=0 NormalX=0 NormalY=0 NormalZ=1 AngleXU=0 Radius=1
    g297: Circle CenterX=46.0728 CenterY=105.865 CenterZ=0 NormalX=0 NormalY=0 NormalZ=1 AngleXU=0 Radius=1
    g298: Circle CenterX=42.0728 CenterY=105.865 CenterZ=0 NormalX=0 NormalY=0 NormalZ=1 AngleXU=0 Radius=1
    g299: BSplineCurve PolesCount=3 KnotsCount=2 Degree=2 IsPeriodic=0
    g300: GeomPoint X=46.0728 Y=109.865 Z=0
    g301: GeomPoint X=42.0728 Y=105.865 Z=0
    g302: Circle CenterX=35.5028 CenterY=105.865 CenterZ=0 NormalX=0 NormalY=0 NormalZ=1 AngleXU=0 Radius=1
    g303: Circle CenterX=31.5028 CenterY=105.865 CenterZ=0 NormalX=0 NormalY=0 NormalZ=1 AngleXU=0 Radius=1
    g304: Circle CenterX=27.9965 CenterY=107.79 CenterZ=0 NormalX=0 NormalY=0 NormalZ=1 AngleXU=0 Radius=1
    g305: BSplineCurve PolesCount=3 KnotsCount=2 Degree=2 IsPeriodic=0
    g306: GeomPoint X=35.5028 Y=105.865 Z=0
    g307: GeomPoint X=27.9965 Y=107.79 Z=0
    g308: LineSegment StartX=2.07281 StartY=124.221 StartZ=0 EndX=42.0728 EndY=124.221 EndZ=0
    g309: LineSegment StartX=46.0728 StartY=120.221 StartZ=0 EndX=46.0728 EndY=109.865 EndZ=0
    g310: LineSegment StartX=42.0728 StartY=105.865 StartZ=0 EndX=35.5028 EndY=105.865 EndZ=0
    g311: LineSegment StartX=27.9965 StartY=107.79 StartZ=0 EndX=1.57905 EndY=122.295 EndZ=0
    g312: Circle CenterX=42.5666 CenterY=-67.3492 CenterZ=0 NormalX=0 NormalY=0 NormalZ=1 AngleXU=0 Radius=1
    g313: Circle CenterX=46.0728 CenterY=-65.424 CenterZ=0 NormalX=0 NormalY=0 NormalZ=1 AngleXU=0 Radius=1
    g314: Circle CenterX=46.0728 CenterY=-69.424 CenterZ=0 NormalX=0 NormalY=0 NormalZ=1 AngleXU=0 Radius=1
    g315: BSplineCurve PolesCount=3 KnotsCount=2 Degree=2 IsPeriodic=0
    g316: GeomPoint X=42.5666 Y=-67.3492 Z=0
    g317: GeomPoint X=46.0728 Y=-69.424 Z=0
    g318: Circle CenterX=46.0728 CenterY=-87.7794 CenterZ=0 NormalX=0 NormalY=0 NormalZ=1 AngleXU=0 Radius=1
    g319: Circle CenterX=46.0728 CenterY=-91.7794 CenterZ=0 NormalX=0 NormalY=0 NormalZ=1 AngleXU=0 Radius=1
    g320: Circle CenterX=42.0728 CenterY=-91.7794 CenterZ=0 NormalX=0 NormalY=0 NormalZ=1 AngleXU=0 Radius=1
    g321: BSplineCurve PolesCount=3 KnotsCount=2 Degree=2 IsPeriodic=0
    g322: GeomPoint X=46.0728 Y=-87.7794 Z=0
    g323: GeomPoint X=42.0728 Y=-91.7794 Z=0
    g324: Circle CenterX=2.07281 CenterY=-91.7794 CenterZ=0 NormalX=0 NormalY=0 NormalZ=1 AngleXU=0 Radius=1
    g325: Circle CenterX=-1.92719 CenterY=-91.7794 CenterZ=0 NormalX=0 NormalY=0 NormalZ=1 AngleXU=0 Radius=1
    g326: Circle CenterX=1.57905 CenterY=-89.8542 CenterZ=0 NormalX=0 NormalY=0 NormalZ=1 AngleXU=0 Radius=1
    g327: BSplineCurve PolesCount=3 KnotsCount=2 Degree=2 IsPeriodic=0
    g328: GeomPoint X=2.07281 Y=-91.7794 Z=0
    g329: GeomPoint X=1.57905 Y=-89.8542 Z=0
    g330: LineSegment StartX=2.07281 StartY=-91.7794 StartZ=0 EndX=42.0728 EndY=-91.7794 EndZ=0
    g331: LineSegment StartX=46.0728 StartY=-87.7794 StartZ=0 EndX=46.0728 EndY=-69.424 EndZ=0
    g332: LineSegment StartX=42.5666 StartY=-67.3492 StartZ=0 EndX=1.57905 EndY=-89.8542 EndZ=0
    g333: Circle CenterX=322.073 CenterY=76.4095 CenterZ=0 NormalX=0 NormalY=0 NormalZ=1 AngleXU=0 Radius=4
    g334: BSplineCurve PolesCount=3 KnotsCount=2 Degree=2 IsPeriodic=0
    g335: GeomPoint X=318.073 Y=72.4095 Z=0
    g336: GeomPoint X=322.073 Y=76.4095 Z=0
    g337: Circle CenterX=375.073 CenterY=72.4095 CenterZ=0 NormalX=0 NormalY=0 NormalZ=1 AngleXU=0 Radius=1
    g338: Circle CenterX=375.073 CenterY=76.4095 CenterZ=0 NormalX=0 NormalY=0 NormalZ=1 AngleXU=0 Radius=1
    g339: Circle CenterX=371.073 CenterY=76.4095 CenterZ=0 NormalX=0 NormalY=0 NormalZ=1 AngleXU=0 Radius=1
    g340: BSplineCurve PolesCount=3 KnotsCount=2 Degree=2 IsPeriodic=0
    g341: GeomPoint X=375.073 Y=72.4095 Z=0
    g342: GeomPoint X=371.073 Y=76.4095 Z=0
    g343: LineSegment StartX=322.073 StartY=76.4095 StartZ=0 EndX=371.073 EndY=76.4095 EndZ=0
    g344: LineSegment StartX=318.073 StartY=72.4095 StartZ=0 EndX=318.073 EndY=-47.4805 EndZ=0
    g345: LineSegment StartX=375.073 StartY=72.4095 StartZ=0 EndX=375.073 EndY=-78.7896 EndZ=0
    g346: ArcOfCircle CenterX=-26.9272 CenterY=22.1087 CenterZ=0 NormalX=0 NormalY=0 NormalZ=1 AngleXU=0 Radius=4 StartAngle=5e-16 EndAngle=3.14159
    g347: LineSegment StartX=-30.9272 StartY=22.1087 StartZ=0 EndX=-34.9272 EndY=-83.7794 EndZ=0
    g348: LineSegment StartX=-18.9272 StartY=-83.7794 StartZ=0 EndX=-22.9272 EndY=22.1087 EndZ=0
  constraints (572):
    c: Coincident(g0,g2)
    c: Block(g0)
    c: Block(g1)
    c: Vertical(g3)
    c: Vertical(g4)
    c: Block(g4)
    c: Block(g3)
    c: Tangent(g6,g7) = 1.5708
    c: Tangent(g7,g9) = 1.5708
    c: Equal(g6,g9)
    c: Coincident(g8,g6)
    c: Coincident(g8,g9)
    c: Block(g7)
    c: Block(g8)
    c: Weight(g10) = 1
    c: Equal(g10,g11)
    c: Equal(g10,g12)
    c: InternalAlignment(g10,g13)
    c: InternalAlignment(g11,g13)
    c: InternalAlignment(g12,g13)
    c: InternalAlignment(g14,g13)
    c: InternalAlignment(g15,g13)
    c: Weight(g16) = 1
    c: Equal(g16,g17)
    c: Equal(g16,g18)
    c: InternalAlignment(g16,g19)
    c: InternalAlignment(g17,g19)
    c: InternalAlignment(g18,g19)
    c: InternalAlignment(g20,g19)
    c: InternalAlignment(g21,g19)
    c: Block(g19)
    c: Block(g13)
    c: Weight(g22) = 1
    c: Equal(g22,g23)
    c: Equal(g22,g24)
    c: InternalAlignment(g22,g25)
    c: InternalAlignment(g23,g25)
    c: InternalAlignment(g24,g25)
    c: InternalAlignment(g26,g25)
    c: InternalAlignment(g27,g25)
    c: Weight(g28) = 1
    c: Equal(g28,g29)
    c: Equal(g28,g30)
    c: InternalAlignment(g28,g31)
    c: InternalAlignment(g29,g31)
    c: InternalAlignment(g30,g31)
    c: InternalAlignment(g32,g31)
    c: InternalAlignment(g33,g31)
    c: Block(g31)
    c: Block(g25)
    c: Weight(g34) = 1
    c: Equal(g34,g35)
    c: Equal(g34,g36)
    c: InternalAlignment(g34,g37)
    c: InternalAlignment(g35,g37)
    c: InternalAlignment(g36,g37)
    c: InternalAlignment(g38,g37)
    c: InternalAlignment(g39,g37)
    c: Weight(g40) = 1
    c: Equal(g40,g41)
    c: Equal(g40,g42)
    c: InternalAlignment(g40,g43)
    c: InternalAlignment(g41,g43)
    c: InternalAlignment(g42,g43)
    c: InternalAlignment(g44,g43)
    c: InternalAlignment(g45,g43)
    c: Block(g37)
    c: Block(g43)
    c: Coincident(g46,g4)
    c: Coincident(g46,g3)
    c: Horizontal(g46)
    c: Distance(g46) = 450
    c: Coincident(g47,g4)
    c: Coincident(g47,g3)
    c: Horizontal(g47)
    c: Horizontal(g48)
    c: Coincident(g2,g48)
    c: Block(g48)
    c: Coincident(g1,g48)
    c: Weight(g49) = 1
    c: Equal(g49,g50)
    c: Equal(g49,g51)
    c: InternalAlignment(g49,g52)
    c: InternalAlignment(g50,g52)
    c: InternalAlignment(g51,g52)
    c: InternalAlignment(g53,g52)
    c: InternalAlignment(g54,g52)
    c: Block(g52)
    c: Weight(g55) = 1
    c: Equal(g55,g56)
    c: Equal(g55,g57)
    c: InternalAlignment(g55,g58)
    c: InternalAlignment(g56,g58)
    c: InternalAlignment(g57,g58)
    c: InternalAlignment(g59,g58)
    c: InternalAlignment(g60,g58)
    c: Block(g58)
    c: Weight(g61) = 1
    c: Equal(g61,g62)
    c: Equal(g61,g63)
    c: InternalAlignment(g61,g64)
    c: InternalAlignment(g62,g64)
    c: InternalAlignment(g63,g64)
    c: InternalAlignment(g65,g64)
    c: InternalAlignment(g66,g64)
    c: Block(g64)
    c: Weight(g67) = 1
    c: Equal(g67,g68)
    c: Equal(g67,g69)
    c: InternalAlignment(g67,g70)
    c: InternalAlignment(g68,g70)
    c: InternalAlignment(g69,g70)
    c: InternalAlignment(g71,g70)
    c: InternalAlignment(g72,g70)
    c: Block(g70)
    c: Weight(g73) = 1
    c: Equal(g73,g74)
    c: Equal(g73,g75)
    c: InternalAlignment(g73,g76)
    c: InternalAlignment(g74,g76)
    c: InternalAlignment(g75,g76)
    c: InternalAlignment(g77,g76)
    c: InternalAlignment(g78,g76)
    c: Weight(g79) = 1
    c: Equal(g79,g80)
    c: Equal(g79,g81)
    c: InternalAlignment(g79,g82)
    c: InternalAlignment(g80,g82)
    c: InternalAlignment(g81,g82)
    c: InternalAlignment(g83,g82)
    c: InternalAlignment(g84,g82)
    c: Block(g76)
    c: Block(g82)
    c: Coincident(g85,g76)
    c: Coincident(g85,g82)
    c: Vertical(g85)
    c: Coincident(g86,g76)
    c: Coincident(g86,g58)
    c: Coincident(g87,g58)
    c: Coincident(g87,g82)
    c: Weight(g88) = 1
    c: Equal(g88,g89)
    c: Equal(g88,g90)
    c: InternalAlignment(g88,g91)
    c: InternalAlignment(g89,g91)
    c: InternalAlignment(g90,g91)
    c: InternalAlignment(g92,g91)
    c: InternalAlignment(g93,g91)
    c: Weight(g94) = 1
    c: Equal(g94,g95)
    c: Equal(g94,g96)
    c: InternalAlignment(g94,g97)
    c: InternalAlignment(g95,g97)
    c: InternalAlignment(g96,g97)
    c: InternalAlignment(g98,g97)
    c: InternalAlignment(g99,g97)
    c: Block(g91)
    c: Block(g97)
    c: Coincident(g100,g91)
    c: Coincident(g100,g97)
    c: Vertical(g100)
    c: Coincident(g101,g91)
    c: Coincident(g101,g52)
    c: Coincident(g102,g52)
    c: Coincident(g102,g97)
    c: Weight(g103) = 1
    c: Equal(g103,g104)
    c: Equal(g103,g105)
    c: InternalAlignment(g103,g106)
    c: InternalAlignment(g104,g106)
    c: InternalAlignment(g105,g106)
    c: InternalAlignment(g107,g106)
    c: InternalAlignment(g108,g106)
    c: Weight(g109) = 1
    c: Equal(g109,g110)
    c: Equal(g109,g111)
    c: InternalAlignment(g109,g112)
    c: InternalAlignment(g110,g112)
    c: InternalAlignment(g111,g112)
    c: InternalAlignment(g113,g112)
    c: InternalAlignment(g114,g112)
    c: Block(g106)
    c: Block(g112)
    c: Coincident(g115,g106)
    c: Coincident(g115,g112)
    c: Vertical(g115)
    c: Coincident(g116,g112)
    c: Coincident(g116,g70)
    c: Coincident(g117,g70)
    c: Coincident(g117,g106)
    c: Weight(g118) = 1
    c: Equal(g118,g119)
    c: Equal(g118,g120)
    c: InternalAlignment(g118,g121)
    c: InternalAlignment(g119,g121)
    c: InternalAlignment(g120,g121)
    c: InternalAlignment(g122,g121)
    c: InternalAlignment(g123,g121)
    c: Weight(g124) = 1
    c: Equal(g124,g125)
    c: Equal(g124,g126)
    c: InternalAlignment(g124,g127)
    c: InternalAlignment(g125,g127)
    c: InternalAlignment(g126,g127)
    c: InternalAlignment(g128,g127)
    c: InternalAlignment(g129,g127)
    c: Block(g121)
    c: Block(g127)
    c: Coincident(g130,g121)
    c: Coincident(g130,g127)
    c: Vertical(g130)
    c: Coincident(g131,g127)
    c: Coincident(g131,g64)
    c: Coincident(g132,g64)
    c: Coincident(g132,g121)
    c: Weight(g133) = 1
    c: Equal(g133,g134)
    c: Equal(g133,g135)
    c: InternalAlignment(g133,g136)
    c: InternalAlignment(g134,g136)
    c: InternalAlignment(g135,g136)
    c: InternalAlignment(g137,g136)
    c: InternalAlignment(g138,g136)
    c: Weight(g139) = 1
    c: Equal(g139,g140)
    c: Equal(g139,g141)
    c: InternalAlignment(g139,g142)
    c: InternalAlignment(g140,g142)
    c: InternalAlignment(g141,g142)
    c: InternalAlignment(g143,g142)
    c: InternalAlignment(g144,g142)
    c: Weight(g145) = 1
    c: Equal(g145,g146)
    c: Equal(g145,g147)
    c: InternalAlignment(g145,g148)
    c: InternalAlignment(g146,g148)
    c: InternalAlignment(g147,g148)
    c: InternalAlignment(g149,g148)
    c: InternalAlignment(g150,g148)
    c: Weight(g151) = 1
    c: Equal(g151,g152)
    c: Equal(g151,g153)
    c: InternalAlignment(g151,g154)
    c: InternalAlignment(g152,g154)
    c: InternalAlignment(g153,g154)
    c: InternalAlignment(g155,g154)
    c: InternalAlignment(g156,g154)
    c: Block(g154)
    c: Block(g148)
    c: Block(g142)
    c: Block(g136)
    c: Coincident(g157,g31)
    c: Coincident(g157,g154)
    c: Coincident(g158,g154)
    c: Coincident(g158,g148)
    c: Horizontal(g158)
    c: Coincident(g159,g148)
    c: Coincident(g159,g31)
    c: Vertical(g159)
    c: Coincident(g160,g25)
    c: Coincident(g160,g142)
    c: Vertical(g160)
    c: Coincident(g161,g142)
    c: Coincident(g161,g136)
    c: Horizontal(g161)
    c: Coincident(g162,g136)
    c: Coincident(g162,g25)
    c: Weight(g163) = 1
    c: Equal(g163,g164)
    c: Equal(g163,g165)
    c: InternalAlignment(g163,g166)
    c: InternalAlignment(g164,g166)
    c: InternalAlignment(g165,g166)
    c: InternalAlignment(g167,g166)
    c: InternalAlignment(g168,g166)
    c: Weight(g169) = 1
    c: Equal(g169,g170)
    c: Equal(g169,g171)
    c: InternalAlignment(g169,g172)
    c: InternalAlignment(g170,g172)
    c: InternalAlignment(g171,g172)
    c: InternalAlignment(g173,g172)
    c: InternalAlignment(g174,g172)
    c: Weight(g175) = 1
    c: Equal(g175,g176)
    c: Equal(g175,g177)
    c: InternalAlignment(g175,g178)
    c: InternalAlignment(g176,g178)
    c: InternalAlignment(g177,g178)
    c: InternalAlignment(g179,g178)
    c: InternalAlignment(g180,g178)
    c: Weight(g181) = 1
    c: Equal(g181,g182)
    c: Equal(g181,g183)
    c: InternalAlignment(g181,g184)
    c: InternalAlignment(g182,g184)
    c: InternalAlignment(g183,g184)
    c: InternalAlignment(g185,g184)
    c: InternalAlignment(g186,g184)
    c: Block(g184)
    c: Block(g178)
    c: Block(g172)
    c: Block(g166)
    c: Coincident(g187,g184)
    c: Coincident(g187,g178)
    c: Horizontal(g187)
    c: Coincident(g188,g178)
    c: Coincident(g188,g13)
    c: Vertical(g188)
    c: Coincident(g189,g19)
    c: Coincident(g189,g172)
    c: Vertical(g189)
    c: Coincident(g190,g172)
    c: Coincident(g190,g166)
    c: Horizontal(g190)
    c: Coincident(g191,g166)
    c: Coincident(g191,g19)
    c: Coincident(g192,g13)
    c: Weight(g193) = 1
    c: Equal(g193,g194)
    c: Equal(g193,g195)
    c: InternalAlignment(g193,g196)
    c: InternalAlignment(g194,g196)
    c: InternalAlignment(g195,g196)
    c: InternalAlignment(g197,g196)
    c: InternalAlignment(g198,g196)
    c: Weight(g199) = 1
    c: Equal(g199,g200)
    c: Equal(g199,g201)
    c: InternalAlignment(g199,g202)
    c: InternalAlignment(g200,g202)
    c: InternalAlignment(g201,g202)
    c: InternalAlignment(g203,g202)
    c: InternalAlignment(g204,g202)
    c: Block(g202)
    c: Block(g196)
    c: Coincident(g205,g202)
    c: Coincident(g205,g37)
    c: Coincident(g206,g37)
    c: Coincident(g206,g196)
    c: Coincident(g207,g196)
    c: Coincident(g207,g202)
    c: Vertical(g207)
    c: Weight(g208) = 1
    c: Equal(g208,g209)
    c: Equal(g208,g210)
    c: InternalAlignment(g208,g211)
    c: InternalAlignment(g209,g211)
    c: InternalAlignment(g210,g211)
    c: InternalAlignment(g212,g211)
    c: InternalAlignment(g213,g211)
    c: Weight(g214) = 1
    c: Equal(g214,g215)
    c: Equal(g214,g216)
    c: InternalAlignment(g214,g217)
    c: InternalAlignment(g215,g217)
    c: InternalAlignment(g216,g217)
    c: InternalAlignment(g218,g217)
    c: InternalAlignment(g219,g217)
    c: Block(g217)
    c: Block(g211)
    c: Coincident(g220,g211)
    c: Coincident(g220,g43)
    c: Coincident(g221,g43)
    c: Coincident(g221,g217)
    c: Coincident(g222,g217)
    c: Coincident(g222,g211)
    c: Vertical(g222)
    c: Horizontal(g223)
    c: Block(g223)
    c: Vertical(g224)
    c: Block(g224)
    c: Block(g225)
    c: Weight(g226) = 1
    c: Equal(g226,g227)
    c: Equal(g226,g228)
    c: InternalAlignment(g226,g229)
    c: InternalAlignment(g227,g229)
    c: InternalAlignment(g228,g229)
    c: InternalAlignment(g230,g229)
    c: InternalAlignment(g231,g229)
    c: Weight(g232) = 1
    c: Equal(g232,g233)
    c: Equal(g232,g234)
    c: InternalAlignment(g232,g235)
    c: InternalAlignment(g233,g235)
    c: InternalAlignment(g234,g235)
    c: InternalAlignment(g236,g235)
    c: InternalAlignment(g237,g235)
    c: Weight(g238) = 1
    c: Equal(g238,g239)
    c: Equal(g238,g240)
    c: InternalAlignment(g238,g241)
    c: InternalAlignment(g239,g241)
    c: InternalAlignment(g240,g241)
    c: InternalAlignment(g242,g241)
    c: InternalAlignment(g243,g241)
    c: Weight(g244) = 1
    c: Equal(g244,g245)
    c: Equal(g244,g246)
    c: InternalAlignment(g244,g247)
    c: InternalAlignment(g245,g247)
    c: InternalAlignment(g246,g247)
    c: InternalAlignment(g248,g247)
    c: InternalAlignment(g249,g247)
    c: Block(g229)
    c: Block(g235)
    c: Block(g241)
    c: Block(g247)
    c: Coincident(g250,g235)
    c: Coincident(g250,g229)
    c: Horizontal(g250)
    c: Block(g192)
    c: Weight(g251) = 1
    c: Equal(g251,g252)
    c: Equal(g251,g253)
    c: InternalAlignment(g251,g254)
    c: InternalAlignment(g252,g254)
    c: InternalAlignment(g253,g254)
    c: InternalAlignment(g255,g254)
    c: InternalAlignment(g256,g254)
    c: Weight(g257) = 1
    c: Equal(g257,g258)
    c: Equal(g257,g259)
    c: InternalAlignment(g257,g260)
    c: InternalAlignment(g258,g260)
    c: InternalAlignment(g259,g260)
    c: InternalAlignment(g261,g260)
    c: InternalAlignment(g262,g260)
    c: Block(g254)
    c: Block(g260)
    c: Coincident(g263,g254)
    c: Coincident(g263,g260)
    c: Weight(g264) = 1
    c: Equal(g264,g265)
    c: Equal(g264,g266)
    c: InternalAlignment(g264,g267)
    c: InternalAlignment(g265,g267)
    c: InternalAlignment(g266,g267)
    c: InternalAlignment(g268,g267)
    c: InternalAlignment(g269,g267)
    c: Weight(g270) = 1
    c: Equal(g270,g271)
    c: Equal(g270,g272)
    c: InternalAlignment(g270,g273)
    c: InternalAlignment(g271,g273)
    c: InternalAlignment(g272,g273)
    c: InternalAlignment(g274,g273)
    c: InternalAlignment(g275,g273)
    c: Weight(g276) = 1
    c: Equal(g276,g277)
    c: Equal(g276,g278)
    c: InternalAlignment(g276,g279)
    c: InternalAlignment(g277,g279)
    c: InternalAlignment(g278,g279)
    c: InternalAlignment(g280,g279)
    c: InternalAlignment(g281,g279)
    c: Block(g279)
    c: Block(g273)
    c: Block(g267)
    c: Coincident(g282,g273)
    c: Coincident(g282,g267)
    c: Coincident(g283,g267)
    c: Coincident(g283,g279)
    c: Vertical(g283)
    c: Coincident(g284,g279)
    c: Coincident(g284,g273)
    c: Horizontal(g284)
    c: Weight(g285) = 1
    c: Equal(g285,g286)
    c: InternalAlignment(g285,g287)
    c: InternalAlignment(g286,g287)
    c: InternalAlignment(g288,g287)
    c: InternalAlignment(g289,g287)
    c: Weight(g290) = 1
    c: InternalAlignment(g291,g293)
    c: InternalAlignment(g292,g293)
    c: InternalAlignment(g294,g293)
    c: InternalAlignment(g295,g293)
    c: Weight(g296) = 1
    c: Equal(g296,g297)
    c: Equal(g296,g298)
    c: InternalAlignment(g296,g299)
    c: InternalAlignment(g297,g299)
    c: InternalAlignment(g298,g299)
    c: InternalAlignment(g300,g299)
    c: InternalAlignment(g301,g299)
    c: Equal(g302,g303)
    c: Equal(g302,g304)
    c: InternalAlignment(g302,g305)
    c: InternalAlignment(g303,g305)
    c: InternalAlignment(g304,g305)
    c: InternalAlignment(g306,g305)
    c: InternalAlignment(g307,g305)
    c: Block(g293)
    c: Block(g299)
    c: Block(g305)
    c: Block(g287)
    c: Coincident(g308,g287)
    c: Coincident(g308,g293)
    c: Horizontal(g308)
    c: Coincident(g309,g293)
    c: Coincident(g309,g299)
    c: Vertical(g309)
    c: Coincident(g310,g299)
    c: Coincident(g310,g305)
    c: Horizontal(g310)
    c: Coincident(g311,g305)
    c: Coincident(g311,g287)
    c: Weight(g312) = 1
    c: Equal(g312,g313)
    c: Equal(g312,g314)
    c: InternalAlignment(g312,g315)
    c: InternalAlignment(g313,g315)
    c: InternalAlignment(g314,g315)
    c: InternalAlignment(g316,g315)
    c: InternalAlignment(g317,g315)
    c: Weight(g318) = 1
    c: Equal(g318,g319)
    c: Equal(g318,g320)
    c: InternalAlignment(g318,g321)
    c: InternalAlignment(g319,g321)
    c: InternalAlignment(g320,g321)
    c: InternalAlignment(g322,g321)
    c: InternalAlignment(g323,g321)
    c: Weight(g324) = 1
    c: Equal(g324,g325)
    c: Equal(g324,g326)
    c: InternalAlignment(g324,g327)
    c: InternalAlignment(g325,g327)
    c: InternalAlignment(g326,g327)
    c: InternalAlignment(g328,g327)
    c: InternalAlignment(g329,g327)
    c: Block(g327)
    c: Block(g321)
    c: Block(g315)
    c: Coincident(g330,g327)
    c: Coincident(g330,g321)
    c: Horizontal(g330)
    c: Coincident(g331,g321)
    c: Coincident(g331,g315)
    c: Vertical(g331)
    c: Coincident(g332,g315)
    c: Coincident(g332,g327)
    c: InternalAlignment(g333,g334)
    c: InternalAlignment(g335,g334)
    c: InternalAlignment(g336,g334)
    c: Block(g334)
    c: Equal(g337,g338)
    c: Equal(g337,g339)
    c: InternalAlignment(g337,g340)
    c: InternalAlignment(g338,g340)
    c: InternalAlignment(g339,g340)
    c: InternalAlignment(g341,g340)
    c: InternalAlignment(g342,g340)
    c: Block(g340)
    c: Coincident(g343,g334)
    c: Horizontal(g343)
    c: Block(g343)
    c: Coincident(g344,g334)
    c: Coincident(g344,g260)
    c: Vertical(g344)
    c: Coincident(g345,g340)
    c: Coincident(g345,g254)
    c: Vertical(g345)
    c: Coincident(g347,g5)
    c: Coincident(g348,g5)
    c: Block(g346)
    c: Block(g5)
    c: Block(g348)
    c: Block(g347)
    c: Distance(g344) = 119.89
FEATURE [Sketcher::SketchObject] Sketch001
  FullyConstrained = true
  MapMode = 4
  Placement = pos=(0,0,0) rot=(0.57735,0.57735,0.57735;2.0944rad)
  Support = -> [Sketch]
  sketch-geometry (46):
    g0: BSplineCurve PolesCount=3 KnotsCount=2 Degree=2 IsPeriodic=0
    g1: ArcOfCircle CenterX=73.1223 CenterY=-32.291 CenterZ=0 NormalX=0 NormalY=0 NormalZ=1 AngleXU=0 Radius=13 StartAngle=5.92268 EndAngle=9.06428
    g2: ArcOfCircle CenterX=66.7816 CenterY=-49.1439 CenterZ=0 NormalX=0 NormalY=0 NormalZ=1 AngleXU=0 Radius=13 StartAngle=2.78068 EndAngle=5.92131
    g3: ArcOfCircle CenterX=55.9263 CenterY=-78.1807 CenterZ=0 NormalX=0 NormalY=0 NormalZ=1 AngleXU=0 Radius=13 StartAngle=5.92268 EndAngle=9.06428
    g4: ArcOfCircle CenterX=49.5884 CenterY=-95.0342 CenterZ=0 NormalX=0 NormalY=0 NormalZ=1 AngleXU=0 Radius=13 StartAngle=2.78068 EndAngle=5.92131
    g5: ArcOfCircle CenterX=38.7206 CenterY=-124.067 CenterZ=0 NormalX=0 NormalY=0 NormalZ=1 AngleXU=0 Radius=13 StartAngle=5.92268 EndAngle=9.06428
    g6: ArcOfCircle CenterX=32.3875 CenterY=-140.92 CenterZ=0 NormalX=0 NormalY=0 NormalZ=1 AngleXU=0 Radius=13 StartAngle=2.78068 EndAngle=5.92131
    g7: ArcOfCircle CenterX=21.4715 CenterY=-169.934 CenterZ=0 NormalX=0 NormalY=0 NormalZ=1 AngleXU=0 Radius=13 StartAngle=5.92268 EndAngle=9.06428
    g8: ArcOfCircle CenterX=15.1336 CenterY=-186.787 CenterZ=0 NormalX=0 NormalY=0 NormalZ=1 AngleXU=0 Radius=13 StartAngle=2.78068 EndAngle=5.92131
    g9-g12: Circle x4 (B-spline internal-alignment scaffolding for g13; pole/knot coordinates omitted)
    g13: BSplineCurve PolesCount=4 KnotsCount=2 Degree=3 IsPeriodic=0
    g14: GeomPoint X=28.8094 Y=-19.0875 Z=0
    g15: GeomPoint X=47.0443 Y=-50.4712 Z=0
    g16: Circle CenterX=53.5586 CenterY=-23.2695 CenterZ=0 NormalX=0 NormalY=0 NormalZ=1 AngleXU=0 Radius=3.24518
    g17: Circle CenterX=-195.441 CenterY=-127.082 CenterZ=0 NormalX=0 NormalY=0 NormalZ=1 AngleXU=0 Radius=1
    g18: Circle CenterX=-8.24091 CenterY=-197.481 CenterZ=0 NormalX=0 NormalY=0 NormalZ=1 AngleXU=0 Radius=1
    g19: Circle CenterX=12.8789 CenterY=-141.321 CenterZ=0 NormalX=0 NormalY=0 NormalZ=1 AngleXU=0 Radius=1
    g20: BSplineCurve PolesCount=3 KnotsCount=2 Degree=2 IsPeriodic=0
    g21: GeomPoint X=-195.441 Y=-127.082 Z=0
    g22: GeomPoint X=12.8789 Y=-141.321 Z=0
    g23: Circle CenterX=-12.8016 CenterY=-179.036 CenterZ=0 NormalX=0 NormalY=0 NormalZ=1 AngleXU=0 Radius=10.5072
    g24: Circle CenterX=0.933922 CenterY=-166.43 CenterZ=0 NormalX=0 NormalY=0 NormalZ=1 AngleXU=0 Radius=3.26661
    g25: Circle CenterX=-33.5518 CenterY=-176.44 CenterZ=0 NormalX=0 NormalY=0 NormalZ=1 AngleXU=0 Radius=5.64388
    g26: Circle CenterX=-47.2366 CenterY=-173.859 CenterZ=0 NormalX=0 NormalY=0 NormalZ=1 AngleXU=0 Radius=3.01653
    g27: Circle CenterX=-56.2595 CenterY=-171.456 CenterZ=0 NormalX=0 NormalY=0 NormalZ=1 AngleXU=0 Radius=2.12826
    g28: ArcOfCircle CenterX=51.2151 CenterY=-198.473 CenterZ=0 NormalX=0 NormalY=0 NormalZ=1 AngleXU=0 Radius=20 StartAngle=2.78189 EndAngle=4.35269
    g29: LineSegment StartX=32.4951 StartY=-191.433 StartZ=0 EndX=94.6578 EndY=-26.1352 EndZ=0
    g30: LineSegment StartX=43.1192 StartY=-220.001 StartZ=0 EndX=-196.497 EndY=-129.89 EndZ=0
    g31: LineSegment StartX=43.1192 StartY=-220.001 StartZ=0 EndX=44.1752 EndY=-217.193 EndZ=0
    g32: LineSegment StartX=117.223 StartY=-19.0875 StartZ=0 EndX=117.223 EndY=-16.0875 EndZ=0
    g33: LineSegment StartX=117.223 StartY=-16.0875 StartZ=0 EndX=17.2232 EndY=-16.0875 EndZ=0
    g34: LineSegment StartX=17.2232 StartY=-16.0875 StartZ=0 EndX=17.2232 EndY=-19.0875 EndZ=0
    g35: LineSegment StartX=28.8094 StartY=-19.0875 StartZ=0 EndX=17.2232 EndY=-19.0875 EndZ=0
    g36: LineSegment StartX=47.0443 StartY=-50.4712 StartZ=0 EndX=12.8789 EndY=-141.321 EndZ=0
    g37: LineSegment StartX=-195.441 StartY=-127.082 StartZ=0 EndX=-196.497 EndY=-129.89 EndZ=0
    g38: LineSegment StartX=85.2866 StartY=-36.8766 StartZ=0 EndX=78.9396 EndY=-53.7463 EndZ=0
    g39: LineSegment StartX=60.9579 StartY=-27.7053 StartZ=0 EndX=54.6191 EndY=-44.5532 EndZ=0
    g40: LineSegment StartX=68.0907 StartY=-82.7664 StartZ=0 EndX=61.7465 EndY=-99.6365 EndZ=0
    g41: LineSegment StartX=43.7619 StartY=-73.595 StartZ=0 EndX=37.426 EndY=-90.4435 EndZ=0
    g42: LineSegment StartX=50.885 StartY=-128.652 StartZ=0 EndX=44.5456 EndY=-145.522 EndZ=0
    g43: LineSegment StartX=26.5562 StartY=-119.481 StartZ=0 EndX=20.2251 EndY=-136.329 EndZ=0
    g44: LineSegment StartX=9.3071 StartY=-165.349 StartZ=0 EndX=2.97115 EndY=-182.197 EndZ=0
    g45: LineSegment StartX=33.6358 StartY=-174.52 StartZ=0 EndX=27.2917 EndY=-191.39 EndZ=0
  constraints (71):
    c: Block(g0)
    c: Block(g1)
    c: Block(g2)
    c: Block(g4)
    c: Block(g3)
    c: Block(g6)
    c: Block(g5)
    c: Block(g8)
    c: Block(g7)
    c: Weight(g9) = 1
    c: Equal(g9,g10)
    c: Equal(g9,g11)
    c: Equal(g9,g12)
    c: InternalAlignment(g9-g12 -> g13) x4
    c: InternalAlignment(g14,g13)
    c: InternalAlignment(g15,g13)
    c: Block(g16)
    c: Weight(g17) = 1
    c: Equal(g17,g18)
    c: Equal(g17,g19)
    c: InternalAlignment(g17,g20)
    c: InternalAlignment(g18,g20)
    c: InternalAlignment(g19,g20)
    c: InternalAlignment(g21,g20)
    c: InternalAlignment(g22,g20)
    c: Block(g20)
    c: Block(g23)
    c: Block(g24)
    c: Block(g25)
    c: Block(g26)
    c: Block(g27)
    c: Block(g28)
    c: Coincident(g29,g28)
    c: Coincident(g29,g0)
    c: Block(g13)
    c: Coincident(g31,g30)
    c: Coincident(g31,g28)
    c: Block(g31)
    c: Coincident(g32,g0)
    c: Vertical(g32)
    c: Coincident(g33,g32)
    c: Horizontal(g33)
    c: Coincident(g34,g33)
    c: Vertical(g34)
    c: Block(g33)
    c: Coincident(g35,g13)
    c: Coincident(g35,g34)
    c: Horizontal(g35)
    c: Coincident(g36,g13)
    c: Coincident(g36,g20)
    c: Coincident(g37,g20)
    c: Coincident(g37,g30)
    c: Block(g30)
    c: Coincident(g38,g1)
    c: Coincident(g38,g2)
    c: Coincident(g39,g1)
    c: Coincident(g39,g2)
    c: Coincident(g40,g3)
    c: Coincident(g40,g4)
    c: Coincident(g41,g3)
    c: Coincident(g41,g4)
    c: Coincident(g42,g5)
    c: Coincident(g42,g6)
    c: Coincident(g43,g5)
    c: Coincident(g43,g6)
    c: Coincident(g44,g7)
    c: Coincident(g44,g8)
    c: Coincident(g45,g7)
    c: Coincident(g45,g8)
    c: Distance(g30) = 256
    c: Distance(g33) = 100
FEATURE [Part::Extrusion] Extrude002
  Base = -> Sketch001
  Dir = (1,0,0)
  DirMode = 2
  FaceMakerClass = Part::FaceMakerBullseye
  LengthFwd = 8
  LengthRev = 0
  Solid = true
  Symmetric = false
FEATURE [Sketcher::SketchObject] Sketch002
  FullyConstrained = true
  sketch-geometry (20):
    g0: LineSegment StartX=-2.77179 StartY=-200.304 StartZ=0 EndX=5.22821 EndY=-200.304 EndZ=0
    g1: LineSegment StartX=5.22821 StartY=-200.304 StartZ=0 EndX=5.22821 EndY=-197.304 EndZ=0
    g2: LineSegment StartX=-2.77179 StartY=-200.304 StartZ=0 EndX=-2.77179 EndY=-197.304 EndZ=0
    g3: LineSegment StartX=5.22821 StartY=-197.304 StartZ=0 EndX=8.22821 EndY=-197.304 EndZ=0
    g4: LineSegment StartX=-2.77179 StartY=-197.304 StartZ=0 EndX=-5.77179 EndY=-197.304 EndZ=0
    g5: LineSegment StartX=19.2282 StartY=-203.304 StartZ=0 EndX=19.2282 EndY=-206.304 EndZ=0
    g6: LineSegment StartX=-16.7718 StartY=-203.304 StartZ=0 EndX=-16.7718 EndY=-206.304 EndZ=0
    g7: LineSegment StartX=-16.7718 StartY=-206.304 StartZ=0 EndX=19.2282 EndY=-206.304 EndZ=0
    g8: Circle CenterX=-16.7718 CenterY=-203.304 CenterZ=0 NormalX=0 NormalY=0 NormalZ=1 AngleXU=0 Radius=1
    g9: Circle CenterX=-5.77179 CenterY=-203.304 CenterZ=0 NormalX=0 NormalY=0 NormalZ=1 AngleXU=0 Radius=1
    g10: Circle CenterX=-5.77179 CenterY=-197.304 CenterZ=0 NormalX=0 NormalY=0 NormalZ=1 AngleXU=0 Radius=1
    g11: BSplineCurve PolesCount=3 KnotsCount=2 Degree=2 IsPeriodic=0
    g12: GeomPoint X=-16.7718 Y=-203.304 Z=0
    g13: GeomPoint X=-5.77179 Y=-197.304 Z=0
    g14: Circle CenterX=19.2282 CenterY=-203.304 CenterZ=0 NormalX=0 NormalY=0 NormalZ=1 AngleXU=0 Radius=1
    g15: Circle CenterX=8.22821 CenterY=-203.304 CenterZ=0 NormalX=0 NormalY=0 NormalZ=1 AngleXU=0 Radius=1
    g16: Circle CenterX=8.22821 CenterY=-197.304 CenterZ=0 NormalX=0 NormalY=0 NormalZ=1 AngleXU=0 Radius=1
    g17: BSplineCurve PolesCount=3 KnotsCount=2 Degree=2 IsPeriodic=0
    g18: GeomPoint X=19.2282 Y=-203.304 Z=0
    g19: GeomPoint X=8.22821 Y=-197.304 Z=0
  constraints (41):
    c: Horizontal(g0)
    c: Distance(g0) = 8
    c: Coincident(g1,g0)
    c: Vertical(g1)
    c: Distance(g1) = 3
    c: Coincident(g2,g0)
    c: Vertical(g2)
    c: Distance(g2) = 3
    c: Coincident(g3,g1)
    c: Horizontal(g3)
    c: Distance(g3) = 3
    c: Coincident(g4,g2)
    c: Horizontal(g4)
    c: Distance(g4) = 3
    c: Vertical(g5)
    c: Vertical(g6)
    c: Coincident(g7,g6)
    c: Coincident(g7,g5)
    c: Weight(g8) = 1
    c: Equal(g8,g9)
    c: Equal(g8,g10)
    c: Coincident(g11,g4)
    c: InternalAlignment(g8,g11)
    c: InternalAlignment(g9,g11)
    c: InternalAlignment(g10,g11)
    c: InternalAlignment(g12,g11)
    c: InternalAlignment(g13,g11)
    c: Coincident(g17,g5)
    c: Weight(g14) = 1
    c: Equal(g14,g15)
    c: Equal(g14,g16)
    c: Coincident(g17,g3)
    c: InternalAlignment(g14,g17)
    c: InternalAlignment(g15,g17)
    c: InternalAlignment(g16,g17)
    c: InternalAlignment(g18,g17)
    c: InternalAlignment(g19,g17)
    c: Block(g7)
    c: Block(g17)
    c: Block(g11)
    c: Block(g6)
FEATURE [Part::Extrusion] Extrude003
  Base = -> Sketch002
  Dir = (0,0,1)
  DirMode = 2
  FaceMakerClass = Part::FaceMakerBullseye
  LengthFwd = 260
  LengthRev = 0
  Solid = true
  Symmetric = false
FEATURE [Sketcher::SketchObject] Sketch003
  FullyConstrained = false
  sketch-geometry (412):
    g0: LineSegment StartX=-42.9272 StartY=136.221 StartZ=0 EndX=-42.9272 EndY=-103.779 EndZ=0
    g1: LineSegment StartX=407.073 StartY=136.221 StartZ=0 EndX=407.073 EndY=-103.779 EndZ=0
    g2: ArcOfCircle CenterX=-26.9272 CenterY=-83.7794 CenterZ=0 NormalX=0 NormalY=0 NormalZ=1 AngleXU=0 Radius=8 StartAngle=3.14159 EndAngle=6.28319
    g3: ArcOfCircle CenterX=391.073 CenterY=-83.7794 CenterZ=0 NormalX=0 NormalY=0 NormalZ=1 AngleXU=0 Radius=8 StartAngle=3.14159 EndAngle=6.28319
    g4: Circle CenterX=175.022 CenterY=27.0628 CenterZ=0 NormalX=0 NormalY=0 NormalZ=1 AngleXU=0 Radius=1
    g5: Circle CenterX=179.022 CenterY=24.8665 CenterZ=0 NormalX=0 NormalY=0 NormalZ=1 AngleXU=0 Radius=1
    g6: Circle CenterX=179.022 CenterY=27.0628 CenterZ=0 NormalX=0 NormalY=0 NormalZ=1 AngleXU=0 Radius=1
    g7: BSplineCurve PolesCount=3 KnotsCount=2 Degree=2 IsPeriodic=0
    g8: GeomPoint X=175.022 Y=27.0628 Z=0
    g9: GeomPoint X=179.022 Y=27.0628 Z=0
    g10: Circle CenterX=189.124 CenterY=27.0628 CenterZ=0 NormalX=0 NormalY=0 NormalZ=1 AngleXU=0 Radius=1
    g11: Circle CenterX=185.124 CenterY=24.8665 CenterZ=0 NormalX=0 NormalY=0 NormalZ=1 AngleXU=0 Radius=1
    g12: Circle CenterX=185.124 CenterY=27.0628 CenterZ=0 NormalX=0 NormalY=0 NormalZ=1 AngleXU=0 Radius=1
    g13: BSplineCurve PolesCount=3 KnotsCount=2 Degree=2 IsPeriodic=0
    g14: GeomPoint X=189.124 Y=27.0628 Z=0
    g15: GeomPoint X=185.124 Y=27.0628 Z=0
    g16: Circle CenterX=175.022 CenterY=5.37834 CenterZ=0 NormalX=0 NormalY=0 NormalZ=1 AngleXU=0 Radius=1
    g17: Circle CenterX=179.022 CenterY=7.57463 CenterZ=0 NormalX=0 NormalY=0 NormalZ=1 AngleXU=0 Radius=1
    g18: Circle CenterX=179.022 CenterY=5.34704 CenterZ=0 NormalX=0 NormalY=0 NormalZ=1 AngleXU=0 Radius=1
    g19: BSplineCurve PolesCount=3 KnotsCount=2 Degree=2 IsPeriodic=0
    g20: GeomPoint X=175.022 Y=5.37834 Z=0
    g21: GeomPoint X=179.022 Y=5.34704 Z=0
    g22: Circle CenterX=189.124 CenterY=5.37834 CenterZ=0 NormalX=0 NormalY=0 NormalZ=1 AngleXU=0 Radius=1
    g23: Circle CenterX=185.124 CenterY=7.57463 CenterZ=0 NormalX=0 NormalY=0 NormalZ=1 AngleXU=0 Radius=1
    g24: Circle CenterX=185.124 CenterY=5.34704 CenterZ=0 NormalX=0 NormalY=0 NormalZ=1 AngleXU=0 Radius=1
    g25: BSplineCurve PolesCount=3 KnotsCount=2 Degree=2 IsPeriodic=0
    g26: GeomPoint X=189.124 Y=5.37834 Z=0
    g27: GeomPoint X=185.124 Y=5.34704 Z=0
    g28: Circle CenterX=165.871 CenterY=18.1458 CenterZ=0 NormalX=0 NormalY=0 NormalZ=1 AngleXU=0 Radius=1
    g29: Circle CenterX=169.377 CenterY=16.2206 CenterZ=0 NormalX=0 NormalY=0 NormalZ=1 AngleXU=0 Radius=1
    g30: Circle CenterX=165.871 CenterY=14.2954 CenterZ=0 NormalX=0 NormalY=0 NormalZ=1 AngleXU=0 Radius=1
    g31: BSplineCurve PolesCount=3 KnotsCount=2 Degree=2 IsPeriodic=0
    g32: GeomPoint X=165.871 Y=18.1458 Z=0
    g33: GeomPoint X=165.871 Y=14.2954 Z=0
    g34: Circle CenterX=198.275 CenterY=18.1458 CenterZ=0 NormalX=0 NormalY=0 NormalZ=1 AngleXU=0 Radius=1
    g35: Circle CenterX=194.768 CenterY=16.2206 CenterZ=0 NormalX=0 NormalY=0 NormalZ=1 AngleXU=0 Radius=1
    g36: Circle CenterX=198.275 CenterY=14.2954 CenterZ=0 NormalX=0 NormalY=0 NormalZ=1 AngleXU=0 Radius=1
    g37: BSplineCurve PolesCount=3 KnotsCount=2 Degree=2 IsPeriodic=0
    g38: GeomPoint X=198.275 Y=18.1458 Z=0
    g39: GeomPoint X=198.275 Y=14.2954 Z=0
    g40: LineSegment StartX=407.073 StartY=-103.779 StartZ=0 EndX=-42.9272 EndY=-103.779 EndZ=0
    g41: Circle CenterX=125.607 CenterY=54.1951 CenterZ=0 NormalX=0 NormalY=0 NormalZ=1 AngleXU=0 Radius=1
    g42: Circle CenterX=139.632 CenterY=46.4944 CenterZ=0 NormalX=0 NormalY=0 NormalZ=1 AngleXU=0 Radius=1
    g43: Circle CenterX=127.326 CenterY=56.7187 CenterZ=0 NormalX=0 NormalY=0 NormalZ=1 AngleXU=0 Radius=1
    g44: BSplineCurve PolesCount=3 KnotsCount=2 Degree=2 IsPeriodic=0
    g45: GeomPoint X=125.607 Y=54.1951 Z=0
    g46: GeomPoint X=127.326 Y=56.7187 Z=0
    g47: Circle CenterX=236.821 CenterY=56.7187 CenterZ=0 NormalX=0 NormalY=0 NormalZ=1 AngleXU=0 Radius=1
    g48: Circle CenterX=224.513 CenterY=46.4944 CenterZ=0 NormalX=0 NormalY=0 NormalZ=1 AngleXU=0 Radius=1
    g49: Circle CenterX=238.538 CenterY=54.1951 CenterZ=0 NormalX=0 NormalY=0 NormalZ=1 AngleXU=0 Radius=1
    g50: BSplineCurve PolesCount=3 KnotsCount=2 Degree=2 IsPeriodic=0
    g51: GeomPoint X=236.821 Y=56.7187 Z=0
    g52: GeomPoint X=238.538 Y=54.1951 Z=0
    g53: Circle CenterX=238.538 CenterY=-21.7539 CenterZ=0 NormalX=0 NormalY=0 NormalZ=1 AngleXU=0 Radius=1
    g54: Circle CenterX=224.513 CenterY=-14.0532 CenterZ=0 NormalX=0 NormalY=0 NormalZ=1 AngleXU=0 Radius=1
    g55: Circle CenterX=236.821 CenterY=-24.2775 CenterZ=0 NormalX=0 NormalY=0 NormalZ=1 AngleXU=0 Radius=1
    g56: BSplineCurve PolesCount=3 KnotsCount=2 Degree=2 IsPeriodic=0
    g57: GeomPoint X=238.538 Y=-21.7539 Z=0
    g58: GeomPoint X=236.821 Y=-24.2775 Z=0
    g59: Circle CenterX=125.607 CenterY=-21.7539 CenterZ=0 NormalX=0 NormalY=0 NormalZ=1 AngleXU=0 Radius=1
    g60: Circle CenterX=139.632 CenterY=-14.0532 CenterZ=0 NormalX=0 NormalY=0 NormalZ=1 AngleXU=0 Radius=1
    g61: Circle CenterX=127.325 CenterY=-24.2775 CenterZ=0 NormalX=0 NormalY=0 NormalZ=1 AngleXU=0 Radius=1
    g62: BSplineCurve PolesCount=3 KnotsCount=2 Degree=2 IsPeriodic=0
    g63: GeomPoint X=125.607 Y=-21.7539 Z=0
    g64: GeomPoint X=127.325 Y=-24.2775 Z=0
    g65: Circle CenterX=302.996 CenterY=111.695 CenterZ=0 NormalX=0 NormalY=0 NormalZ=1 AngleXU=0 Radius=1
    g66: Circle CenterX=306.073 CenterY=114.251 CenterZ=0 NormalX=0 NormalY=0 NormalZ=1 AngleXU=0 Radius=1
    g67: Circle CenterX=306.073 CenterY=110.251 CenterZ=0 NormalX=0 NormalY=0 NormalZ=1 AngleXU=0 Radius=1
    g68: BSplineCurve PolesCount=3 KnotsCount=2 Degree=2 IsPeriodic=0
    g69: GeomPoint X=302.996 Y=111.695 Z=0
    g70: GeomPoint X=306.073 Y=110.251 Z=0
    g71: Circle CenterX=306.073 CenterY=95.2763 CenterZ=0 NormalX=0 NormalY=0 NormalZ=1 AngleXU=0 Radius=1
    g72: Circle CenterX=306.073 CenterY=91.2763 CenterZ=0 NormalX=0 NormalY=0 NormalZ=1 AngleXU=0 Radius=1
    g73: Circle CenterX=302.567 CenterY=89.3511 CenterZ=0 NormalX=0 NormalY=0 NormalZ=1 AngleXU=0 Radius=1
    g74: BSplineCurve PolesCount=3 KnotsCount=2 Degree=2 IsPeriodic=0
    g75: GeomPoint X=306.073 Y=95.2763 Z=0
    g76: GeomPoint X=302.567 Y=89.3511 Z=0
    g77: LineSegment StartX=306.073 StartY=110.251 StartZ=0 EndX=306.073 EndY=95.2763 EndZ=0
    g78: LineSegment StartX=302.996 StartY=111.695 StartZ=0 EndX=236.821 EndY=56.7187 EndZ=0
    g79: LineSegment StartX=238.538 StartY=54.1951 StartZ=0 EndX=302.567 EndY=89.3511 EndZ=0
    g80: Circle CenterX=61.1496 CenterY=111.695 CenterZ=0 NormalX=0 NormalY=0 NormalZ=1 AngleXU=0 Radius=1
    g81: Circle CenterX=58.0728 CenterY=114.251 CenterZ=0 NormalX=0 NormalY=0 NormalZ=1 AngleXU=0 Radius=1
    g82: Circle CenterX=58.0728 CenterY=110.251 CenterZ=0 NormalX=0 NormalY=0 NormalZ=1 AngleXU=0 Radius=1
    g83: BSplineCurve PolesCount=3 KnotsCount=2 Degree=2 IsPeriodic=0
    g84: GeomPoint X=61.1496 Y=111.695 Z=0
    g85: GeomPoint X=58.0728 Y=110.251 Z=0
    g86: Circle CenterX=61.5791 CenterY=89.3511 CenterZ=0 NormalX=0 NormalY=0 NormalZ=1 AngleXU=0 Radius=1
    g87: Circle CenterX=58.0728 CenterY=91.2763 CenterZ=0 NormalX=0 NormalY=0 NormalZ=1 AngleXU=0 Radius=1
    g88: Circle CenterX=58.0728 CenterY=95.2763 CenterZ=0 NormalX=0 NormalY=0 NormalZ=1 AngleXU=0 Radius=1
    g89: BSplineCurve PolesCount=3 KnotsCount=2 Degree=2 IsPeriodic=0
    g90: GeomPoint X=61.5791 Y=89.3511 Z=0
    g91: GeomPoint X=58.0728 Y=95.2763 Z=0
    g92: LineSegment StartX=58.0728 StartY=110.251 StartZ=0 EndX=58.0728 EndY=95.2763 EndZ=0
    g93: LineSegment StartX=61.1496 StartY=111.695 StartZ=0 EndX=127.326 EndY=56.7187 EndZ=0
    g94: LineSegment StartX=125.607 StartY=54.1951 StartZ=0 EndX=61.5791 EndY=89.3511 EndZ=0
    g95: Circle CenterX=61.5791 CenterY=-56.9099 CenterZ=0 NormalX=0 NormalY=0 NormalZ=1 AngleXU=0 Radius=1
    g96: Circle CenterX=58.0728 CenterY=-58.8351 CenterZ=0 NormalX=0 NormalY=0 NormalZ=1 AngleXU=0 Radius=1
    g97: Circle CenterX=58.0728 CenterY=-62.8351 CenterZ=0 NormalX=0 NormalY=0 NormalZ=1 AngleXU=0 Radius=1
    g98: BSplineCurve PolesCount=3 KnotsCount=2 Degree=2 IsPeriodic=0
    g99: GeomPoint X=61.5791 Y=-56.9099 Z=0
    g100: GeomPoint X=58.0728 Y=-62.8351 Z=0
    g101: Circle CenterX=58.0728 CenterY=-77.8102 CenterZ=0 NormalX=0 NormalY=0 NormalZ=1 AngleXU=0 Radius=1
    g102: Circle CenterX=58.0728 CenterY=-81.8102 CenterZ=0 NormalX=0 NormalY=0 NormalZ=1 AngleXU=0 Radius=1
    g103: Circle CenterX=61.1496 CenterY=-79.2541 CenterZ=0 NormalX=0 NormalY=0 NormalZ=1 AngleXU=0 Radius=1
    g104: BSplineCurve PolesCount=3 KnotsCount=2 Degree=2 IsPeriodic=0
    g105: GeomPoint X=58.0728 Y=-77.8102 Z=0
    g106: GeomPoint X=61.1496 Y=-79.2541 Z=0
    g107: LineSegment StartX=58.0728 StartY=-62.8351 StartZ=0 EndX=58.0728 EndY=-77.8102 EndZ=0
    g108: LineSegment StartX=61.1496 StartY=-79.2541 StartZ=0 EndX=127.325 EndY=-24.2775 EndZ=0
    g109: LineSegment StartX=125.607 StartY=-21.7539 StartZ=0 EndX=61.5791 EndY=-56.9099 EndZ=0
    g110: Circle CenterX=302.567 CenterY=-56.9099 CenterZ=0 NormalX=0 NormalY=0 NormalZ=1 AngleXU=0 Radius=1
    g111: Circle CenterX=306.073 CenterY=-58.8351 CenterZ=0 NormalX=0 NormalY=0 NormalZ=1 AngleXU=0 Radius=1
    g112: Circle CenterX=306.073 CenterY=-62.8351 CenterZ=0 NormalX=0 NormalY=0 NormalZ=1 AngleXU=0 Radius=1
    g113: BSplineCurve PolesCount=3 KnotsCount=2 Degree=2 IsPeriodic=0
    g114: GeomPoint X=302.567 Y=-56.9099 Z=0
    g115: GeomPoint X=306.073 Y=-62.8351 Z=0
    g116: Circle CenterX=302.996 CenterY=-79.2541 CenterZ=0 NormalX=0 NormalY=0 NormalZ=1 AngleXU=0 Radius=1
    g117: Circle CenterX=306.073 CenterY=-81.8102 CenterZ=0 NormalX=0 NormalY=0 NormalZ=1 AngleXU=0 Radius=1
    g118: Circle CenterX=306.073 CenterY=-77.8102 CenterZ=0 NormalX=0 NormalY=0 NormalZ=1 AngleXU=0 Radius=1
    g119: BSplineCurve PolesCount=3 KnotsCount=2 Degree=2 IsPeriodic=0
    g120: GeomPoint X=302.996 Y=-79.2541 Z=0
    g121: GeomPoint X=306.073 Y=-77.8102 Z=0
    g122: LineSegment StartX=306.073 StartY=-62.8351 StartZ=0 EndX=306.073 EndY=-77.8102 EndZ=0
    g123: LineSegment StartX=302.996 StartY=-79.2541 StartZ=0 EndX=236.821 EndY=-24.2775 EndZ=0
    g124: LineSegment StartX=238.538 StartY=-21.7539 StartZ=0 EndX=302.567 EndY=-56.9099 EndZ=0
    g125: Circle CenterX=61.6457 CenterY=-88.8112 CenterZ=0 NormalX=0 NormalY=0 NormalZ=1 AngleXU=0 Radius=1
    g126: Circle CenterX=58.0728 CenterY=-91.7794 CenterZ=0 NormalX=0 NormalY=0 NormalZ=1 AngleXU=0 Radius=1
    g127: Circle CenterX=63.9135 CenterY=-91.7791 CenterZ=0 NormalX=0 NormalY=0 NormalZ=1 AngleXU=0 Radius=1
    g128: BSplineCurve PolesCount=3 KnotsCount=2 Degree=2 IsPeriodic=0
    g129: GeomPoint X=61.6457 Y=-88.8112 Z=0
    g130: GeomPoint X=63.9135 Y=-91.7791 Z=0
    g131: Circle CenterX=179.022 CenterY=-85.8163 CenterZ=0 NormalX=0 NormalY=0 NormalZ=1 AngleXU=0 Radius=1
    g132: Circle CenterX=179.022 CenterY=-91.7794 CenterZ=0 NormalX=0 NormalY=0 NormalZ=1 AngleXU=0 Radius=1
    g133: Circle CenterX=171.895 CenterY=-91.7791 CenterZ=0 NormalX=0 NormalY=0 NormalZ=1 AngleXU=0 Radius=1
    g134: BSplineCurve PolesCount=3 KnotsCount=2 Degree=2 IsPeriodic=0
    g135: GeomPoint X=179.022 Y=-85.8163 Z=0
    g136: GeomPoint X=171.895 Y=-91.7791 Z=0
    g137: Circle CenterX=185.124 CenterY=-86.2028 CenterZ=0 NormalX=0 NormalY=0 NormalZ=1 AngleXU=0 Radius=1
    g138: Circle CenterX=185.124 CenterY=-91.7794 CenterZ=0 NormalX=0 NormalY=0 NormalZ=1 AngleXU=0 Radius=1
    g139: Circle CenterX=191.747 CenterY=-91.7794 CenterZ=0 NormalX=0 NormalY=0 NormalZ=1 AngleXU=0 Radius=1
    g140: BSplineCurve PolesCount=3 KnotsCount=2 Degree=2 IsPeriodic=0
    g141: GeomPoint X=185.124 Y=-86.2028 Z=0
    g142: GeomPoint X=191.747 Y=-91.7794 Z=0
    g143: Circle CenterX=299.888 CenterY=-86.6413 CenterZ=0 NormalX=0 NormalY=0 NormalZ=1 AngleXU=0 Radius=1
    g144: Circle CenterX=306.073 CenterY=-91.7794 CenterZ=0 NormalX=0 NormalY=0 NormalZ=1 AngleXU=0 Radius=1
    g145: Circle CenterX=298.776 CenterY=-91.7794 CenterZ=0 NormalX=0 NormalY=0 NormalZ=1 AngleXU=0 Radius=1
    g146: BSplineCurve PolesCount=3 KnotsCount=2 Degree=2 IsPeriodic=0
    g147: GeomPoint X=299.888 Y=-86.6413 Z=0
    g148: GeomPoint X=298.776 Y=-91.7794 Z=0
    g149: LineSegment StartX=189.124 StartY=5.37834 StartZ=0 EndX=299.888 EndY=-86.6413 EndZ=0
    g150: LineSegment StartX=298.776 StartY=-91.7794 StartZ=0 EndX=191.747 EndY=-91.7794 EndZ=0
    g151: LineSegment StartX=185.124 StartY=-86.2028 StartZ=0 EndX=185.124 EndY=5.34704 EndZ=0
    g152: LineSegment StartX=179.022 StartY=5.34704 StartZ=0 EndX=179.022 EndY=-85.8163 EndZ=0
    g153: LineSegment StartX=171.895 StartY=-91.7791 StartZ=0 EndX=63.9135 EndY=-91.7791 EndZ=0
    g154: LineSegment StartX=61.6457 StartY=-88.8112 StartZ=0 EndX=175.022 EndY=5.37834 EndZ=0
    g155: Circle CenterX=302.073 CenterY=124.221 CenterZ=0 NormalX=0 NormalY=0 NormalZ=1 AngleXU=0 Radius=1
    g156: Circle CenterX=306.073 CenterY=124.221 CenterZ=0 NormalX=0 NormalY=0 NormalZ=1 AngleXU=0 Radius=1
    g157: Circle CenterX=302.996 CenterY=121.665 CenterZ=0 NormalX=0 NormalY=0 NormalZ=1 AngleXU=0 Radius=1
    g158: BSplineCurve PolesCount=3 KnotsCount=2 Degree=2 IsPeriodic=0
    g159: GeomPoint X=302.073 Y=124.221 Z=0
    g160: GeomPoint X=302.996 Y=121.665 Z=0
    g161: Circle CenterX=189.124 CenterY=124.221 CenterZ=0 NormalX=0 NormalY=0 NormalZ=1 AngleXU=0 Radius=1
    g162: Circle CenterX=185.124 CenterY=124.221 CenterZ=0 NormalX=0 NormalY=0 NormalZ=1 AngleXU=0 Radius=1
    g163: Circle CenterX=185.124 CenterY=120.221 CenterZ=0 NormalX=0 NormalY=0 NormalZ=1 AngleXU=0 Radius=1
    g164: BSplineCurve PolesCount=3 KnotsCount=2 Degree=2 IsPeriodic=0
    g165: GeomPoint X=189.124 Y=124.221 Z=0
    g166: GeomPoint X=185.124 Y=120.221 Z=0
    g167: Circle CenterX=175.022 CenterY=124.221 CenterZ=0 NormalX=0 NormalY=0 NormalZ=1 AngleXU=0 Radius=1
    g168: Circle CenterX=179.022 CenterY=124.221 CenterZ=0 NormalX=0 NormalY=0 NormalZ=1 AngleXU=0 Radius=1
    g169: Circle CenterX=179.022 CenterY=120.221 CenterZ=0 NormalX=0 NormalY=0 NormalZ=1 AngleXU=0 Radius=1
    g170: BSplineCurve PolesCount=3 KnotsCount=2 Degree=2 IsPeriodic=0
    g171: GeomPoint X=175.022 Y=124.221 Z=0
    g172: GeomPoint X=179.022 Y=120.221 Z=0
    g173: Circle CenterX=62.0728 CenterY=124.221 CenterZ=0 NormalX=0 NormalY=0 NormalZ=1 AngleXU=0 Radius=1
    g174: Circle CenterX=58.0728 CenterY=124.221 CenterZ=0 NormalX=0 NormalY=0 NormalZ=1 AngleXU=0 Radius=1
    g175: Circle CenterX=61.1496 CenterY=121.665 CenterZ=0 NormalX=0 NormalY=0 NormalZ=1 AngleXU=0 Radius=1
    g176: BSplineCurve PolesCount=3 KnotsCount=2 Degree=2 IsPeriodic=0
    g177: GeomPoint X=62.0728 Y=124.221 Z=0
    g178: GeomPoint X=61.1496 Y=121.665 Z=0
    g179: LineSegment StartX=179.022 StartY=120.221 StartZ=0 EndX=179.022 EndY=27.0628 EndZ=0
    g180: LineSegment StartX=185.124 StartY=27.0628 StartZ=0 EndX=185.124 EndY=120.221 EndZ=0
    g181: LineSegment StartX=302.996 StartY=121.665 StartZ=0 EndX=189.124 EndY=27.0628 EndZ=0
    g182: LineSegment StartX=175.022 StartY=27.0628 StartZ=0 EndX=61.1496 EndY=121.665 EndZ=0
    g183: Circle CenterX=61.5791 CenterY=75.4095 CenterZ=0 NormalX=0 NormalY=0 NormalZ=1 AngleXU=0 Radius=1
    g184: Circle CenterX=58.0728 CenterY=77.3346 CenterZ=0 NormalX=0 NormalY=0 NormalZ=1 AngleXU=0 Radius=1
    g185: Circle CenterX=58.0728 CenterY=73.3346 CenterZ=0 NormalX=0 NormalY=0 NormalZ=1 AngleXU=0 Radius=1
    g186: BSplineCurve PolesCount=3 KnotsCount=2 Degree=2 IsPeriodic=0
    g187: GeomPoint X=61.5791 Y=75.4095 Z=0
    g188: GeomPoint X=58.0728 Y=73.3346 Z=0
    g189: Circle CenterX=58.0728 CenterY=-40.8935 CenterZ=0 NormalX=0 NormalY=0 NormalZ=1 AngleXU=0 Radius=1
    g190: Circle CenterX=58.0728 CenterY=-44.8935 CenterZ=0 NormalX=0 NormalY=0 NormalZ=1 AngleXU=0 Radius=1
    g191: Circle CenterX=61.5791 CenterY=-42.9683 CenterZ=0 NormalX=0 NormalY=0 NormalZ=1 AngleXU=0 Radius=1
    g192: BSplineCurve PolesCount=3 KnotsCount=2 Degree=2 IsPeriodic=0
    g193: GeomPoint X=58.0728 Y=-40.8935 Z=0
    g194: GeomPoint X=61.5791 Y=-42.9683 Z=0
    g195: LineSegment StartX=61.5791 StartY=-42.9683 StartZ=0 EndX=165.871 EndY=14.2954 EndZ=0
    g196: LineSegment StartX=165.871 StartY=18.1458 StartZ=0 EndX=61.5791 EndY=75.4095 EndZ=0
    g197: LineSegment StartX=58.0728 StartY=73.3346 StartZ=0 EndX=58.0728 EndY=-40.8935 EndZ=0
    g198: Circle CenterX=302.567 CenterY=-42.9683 CenterZ=0 NormalX=0 NormalY=0 NormalZ=1 AngleXU=0 Radius=1
    g199: Circle CenterX=306.073 CenterY=-44.8935 CenterZ=0 NormalX=0 NormalY=0 NormalZ=1 AngleXU=0 Radius=1
    g200: Circle CenterX=306.073 CenterY=-40.8935 CenterZ=0 NormalX=0 NormalY=0 NormalZ=1 AngleXU=0 Radius=1
    g201: BSplineCurve PolesCount=3 KnotsCount=2 Degree=2 IsPeriodic=0
    g202: GeomPoint X=302.567 Y=-42.9683 Z=0
    g203: GeomPoint X=306.073 Y=-40.8935 Z=0
    g204: Circle CenterX=306.073 CenterY=73.3346 CenterZ=0 NormalX=0 NormalY=0 NormalZ=1 AngleXU=0 Radius=1
    g205: Circle CenterX=306.073 CenterY=77.3346 CenterZ=0 NormalX=0 NormalY=0 NormalZ=1 AngleXU=0 Radius=1
    g206: Circle CenterX=302.567 CenterY=75.4095 CenterZ=0 NormalX=0 NormalY=0 NormalZ=1 AngleXU=0 Radius=1
    g207: BSplineCurve PolesCount=3 KnotsCount=2 Degree=2 IsPeriodic=0
    g208: GeomPoint X=306.073 Y=73.3346 Z=0
    g209: GeomPoint X=302.567 Y=75.4095 Z=0
    g210: LineSegment StartX=302.567 StartY=-42.9683 StartZ=0 EndX=198.275 EndY=14.2954 EndZ=0
    g211: LineSegment StartX=198.275 StartY=18.1458 StartZ=0 EndX=302.567 EndY=75.4095 EndZ=0
    g212: LineSegment StartX=306.073 StartY=73.3346 StartZ=0 EndX=306.073 EndY=-40.8935 EndZ=0
    g213: LineSegment StartX=322.073 StartY=105.865 StartZ=0 EndX=328.643 EndY=105.865 EndZ=0
    g214: LineSegment StartX=318.073 StartY=120.221 StartZ=0 EndX=318.073 EndY=109.865 EndZ=0
    g215: LineSegment StartX=336.157 StartY=107.779 StartZ=0 EndX=362.567 EndY=122.294 EndZ=0
    g216: Circle CenterX=362.073 CenterY=124.221 CenterZ=0 NormalX=0 NormalY=0 NormalZ=1 AngleXU=0 Radius=1
    g217: Circle CenterX=366.073 CenterY=124.221 CenterZ=0 NormalX=0 NormalY=0 NormalZ=1 AngleXU=0 Radius=1
    g218: Circle CenterX=362.567 CenterY=122.294 CenterZ=0 NormalX=0 NormalY=0 NormalZ=1 AngleXU=0 Radius=1
    g219: BSplineCurve PolesCount=3 KnotsCount=2 Degree=2 IsPeriodic=0
    g220: GeomPoint X=362.073 Y=124.221 Z=0
    g221: GeomPoint X=362.567 Y=122.294 Z=0
    g222: Circle CenterX=322.073 CenterY=124.221 CenterZ=0 NormalX=0 NormalY=0 NormalZ=1 AngleXU=0 Radius=1
    g223: Circle CenterX=318.073 CenterY=124.221 CenterZ=0 NormalX=0 NormalY=0 NormalZ=1 AngleXU=0 Radius=1
    g224: Circle CenterX=318.073 CenterY=120.221 CenterZ=0 NormalX=0 NormalY=0 NormalZ=1 AngleXU=0 Radius=1
    g225: BSplineCurve PolesCount=3 KnotsCount=2 Degree=2 IsPeriodic=0
    g226: GeomPoint X=322.073 Y=124.221 Z=0
    g227: GeomPoint X=318.073 Y=120.221 Z=0
    g228: Circle CenterX=322.073 CenterY=105.865 CenterZ=0 NormalX=0 NormalY=0 NormalZ=1 AngleXU=0 Radius=1
    g229: Circle CenterX=318.073 CenterY=105.865 CenterZ=0 NormalX=0 NormalY=0 NormalZ=1 AngleXU=0 Radius=1
    g230: Circle CenterX=318.073 CenterY=109.865 CenterZ=0 NormalX=0 NormalY=0 NormalZ=1 AngleXU=0 Radius=1
    g231: BSplineCurve PolesCount=3 KnotsCount=2 Degree=2 IsPeriodic=0
    g232: GeomPoint X=322.073 Y=105.865 Z=0
    g233: GeomPoint X=318.073 Y=109.865 Z=0
    g234: Circle CenterX=336.157 CenterY=107.779 CenterZ=0 NormalX=0 NormalY=0 NormalZ=1 AngleXU=0 Radius=1
    g235: Circle CenterX=332.651 CenterY=105.853 CenterZ=0 NormalX=0 NormalY=0 NormalZ=1 AngleXU=0 Radius=1
    g236: Circle CenterX=328.643 CenterY=105.865 CenterZ=0 NormalX=0 NormalY=0 NormalZ=1 AngleXU=0 Radius=1
    g237: BSplineCurve PolesCount=3 KnotsCount=2 Degree=2 IsPeriodic=0
    g238: GeomPoint X=336.157 Y=107.779 Z=0
    g239: GeomPoint X=328.643 Y=105.865 Z=0
    g240: LineSegment StartX=322.073 StartY=124.221 StartZ=0 EndX=362.073 EndY=124.221 EndZ=0
    g241: Circle CenterX=371.567 CenterY=-80.8644 CenterZ=0 NormalX=0 NormalY=0 NormalZ=1 AngleXU=0 Radius=1
    g242: Circle CenterX=375.073 CenterY=-82.7896 CenterZ=0 NormalX=0 NormalY=0 NormalZ=1 AngleXU=0 Radius=1
    g243: Circle CenterX=375.073 CenterY=-78.7896 CenterZ=0 NormalX=0 NormalY=0 NormalZ=1 AngleXU=0 Radius=1
    g244: BSplineCurve PolesCount=3 KnotsCount=2 Degree=2 IsPeriodic=0
    g245: GeomPoint X=371.567 Y=-80.8644 Z=0
    g246: GeomPoint X=375.073 Y=-78.7896 Z=0
    g247: Circle CenterX=321.579 CenterY=-53.4075 CenterZ=0 NormalX=0 NormalY=0 NormalZ=1 AngleXU=0 Radius=1
    g248: Circle CenterX=318.073 CenterY=-51.4823 CenterZ=0 NormalX=0 NormalY=0 NormalZ=1 AngleXU=0 Radius=1
    g249: Circle CenterX=318.073 CenterY=-47.4805 CenterZ=0 NormalX=0 NormalY=0 NormalZ=1 AngleXU=0 Radius=1
    g250: BSplineCurve PolesCount=3 KnotsCount=2 Degree=2 IsPeriodic=0
    g251: GeomPoint X=321.579 Y=-53.4075 Z=0
    g252: GeomPoint X=318.073 Y=-47.4805 Z=0
    g253: LineSegment StartX=371.567 StartY=-80.8644 StartZ=0 EndX=321.579 EndY=-53.4075 EndZ=0
    g254: Circle CenterX=321.579 CenterY=-67.3492 CenterZ=0 NormalX=0 NormalY=0 NormalZ=1 AngleXU=0 Radius=1
    g255: Circle CenterX=318.073 CenterY=-65.424 CenterZ=0 NormalX=0 NormalY=0 NormalZ=1 AngleXU=0 Radius=1
    g256: Circle CenterX=318.073 CenterY=-69.424 CenterZ=0 NormalX=0 NormalY=0 NormalZ=1 AngleXU=0 Radius=1
    g257: BSplineCurve PolesCount=3 KnotsCount=2 Degree=2 IsPeriodic=0
    g258: GeomPoint X=321.579 Y=-67.3492 Z=0
    g259: GeomPoint X=318.073 Y=-69.424 Z=0
    g260: Circle CenterX=362.567 CenterY=-89.8542 CenterZ=0 NormalX=0 NormalY=0 NormalZ=1 AngleXU=0 Radius=1
    g261: Circle CenterX=366.073 CenterY=-91.7794 CenterZ=0 NormalX=0 NormalY=0 NormalZ=1 AngleXU=0 Radius=1
    g262: Circle CenterX=362.073 CenterY=-91.7794 CenterZ=0 NormalX=0 NormalY=0 NormalZ=1 AngleXU=0 Radius=1
    g263: BSplineCurve PolesCount=3 KnotsCount=2 Degree=2 IsPeriodic=0
    g264: GeomPoint X=362.567 Y=-89.8542 Z=0
    g265: GeomPoint X=362.073 Y=-91.7794 Z=0
    g266: Circle CenterX=322.073 CenterY=-91.7794 CenterZ=0 NormalX=0 NormalY=0 NormalZ=1 AngleXU=0 Radius=1
    g267: Circle CenterX=318.073 CenterY=-91.7794 CenterZ=0 NormalX=0 NormalY=0 NormalZ=1 AngleXU=0 Radius=1
    g268: Circle CenterX=318.073 CenterY=-87.7794 CenterZ=0 NormalX=0 NormalY=0 NormalZ=1 AngleXU=0 Radius=1
    g269: BSplineCurve PolesCount=3 KnotsCount=2 Degree=2 IsPeriodic=0
    g270: GeomPoint X=322.073 Y=-91.7794 Z=0
    g271: GeomPoint X=318.073 Y=-87.7794 Z=0
    g272: LineSegment StartX=362.567 StartY=-89.8542 StartZ=0 EndX=321.579 EndY=-67.3492 EndZ=0
    g273: LineSegment StartX=318.073 StartY=-69.424 StartZ=0 EndX=318.073 EndY=-87.7794 EndZ=0
    g274: LineSegment StartX=322.073 StartY=-91.7794 StartZ=0 EndX=362.073 EndY=-91.7794 EndZ=0
    g275: Circle CenterX=2.07281 CenterY=124.221 CenterZ=0 NormalX=0 NormalY=0 NormalZ=1 AngleXU=0 Radius=1
    g276: Circle CenterX=1.57905 CenterY=122.295 CenterZ=0 NormalX=0 NormalY=0 NormalZ=1 AngleXU=0 Radius=1
    g277: BSplineCurve PolesCount=3 KnotsCount=2 Degree=2 IsPeriodic=0
    g278: GeomPoint X=2.07281 Y=124.221 Z=0
    g279: GeomPoint X=1.57905 Y=122.295 Z=0
    g280: Circle CenterX=42.0728 CenterY=124.221 CenterZ=0 NormalX=0 NormalY=0 NormalZ=1 AngleXU=0 Radius=1
    g281: Circle CenterX=46.0728 CenterY=124.221 CenterZ=0 NormalX=0 NormalY=0 NormalZ=1 AngleXU=0 Radius=1
    g282: Circle CenterX=46.0728 CenterY=120.221 CenterZ=0 NormalX=0 NormalY=0 NormalZ=1 AngleXU=0 Radius=1
    g283: BSplineCurve PolesCount=3 KnotsCount=2 Degree=2 IsPeriodic=0
    g284: GeomPoint X=42.0728 Y=124.221 Z=0
    g285: GeomPoint X=46.0728 Y=120.221 Z=0
    g286: Circle CenterX=46.0728 CenterY=109.865 CenterZ=0 NormalX=0 NormalY=0 NormalZ=1 AngleXU=0 Radius=1
    g287: Circle CenterX=46.0728 CenterY=105.865 CenterZ=0 NormalX=0 NormalY=0 NormalZ=1 AngleXU=0 Radius=1
    g288: Circle CenterX=42.0728 CenterY=105.865 CenterZ=0 NormalX=0 NormalY=0 NormalZ=1 AngleXU=0 Radius=1
    g289: BSplineCurve PolesCount=3 KnotsCount=2 Degree=2 IsPeriodic=0
    g290: GeomPoint X=46.0728 Y=109.865 Z=0
    g291: GeomPoint X=42.0728 Y=105.865 Z=0
    g292: Circle CenterX=35.5028 CenterY=105.865 CenterZ=0 NormalX=0 NormalY=0 NormalZ=1 AngleXU=0 Radius=1
    g293: Circle CenterX=31.5028 CenterY=105.865 CenterZ=0 NormalX=0 NormalY=0 NormalZ=1 AngleXU=0 Radius=1
    g294: Circle CenterX=27.9965 CenterY=107.79 CenterZ=0 NormalX=0 NormalY=0 NormalZ=1 AngleXU=0 Radius=1
    g295: BSplineCurve PolesCount=3 KnotsCount=2 Degree=2 IsPeriodic=0
    g296: GeomPoint X=35.5028 Y=105.865 Z=0
    g297: GeomPoint X=27.9965 Y=107.79 Z=0
    g298: LineSegment StartX=2.07281 StartY=124.221 StartZ=0 EndX=42.0728 EndY=124.221 EndZ=0
    g299: LineSegment StartX=46.0728 StartY=120.221 StartZ=0 EndX=46.0728 EndY=109.865 EndZ=0
    g300: LineSegment StartX=42.0728 StartY=105.865 StartZ=0 EndX=35.5028 EndY=105.865 EndZ=0
    g301: LineSegment StartX=27.9965 StartY=107.79 StartZ=0 EndX=1.57905 EndY=122.295 EndZ=0
    g302: Circle CenterX=42.5666 CenterY=-67.3492 CenterZ=0 NormalX=0 NormalY=0 NormalZ=1 AngleXU=0 Radius=1
    g303: Circle CenterX=46.0728 CenterY=-65.424 CenterZ=0 NormalX=0 NormalY=0 NormalZ=1 AngleXU=0 Radius=1
    g304: Circle CenterX=46.0728 CenterY=-69.424 CenterZ=0 NormalX=0 NormalY=0 NormalZ=1 AngleXU=0 Radius=1
    g305: BSplineCurve PolesCount=3 KnotsCount=2 Degree=2 IsPeriodic=0
    g306: GeomPoint X=42.5666 Y=-67.3492 Z=0
    g307: GeomPoint X=46.0728 Y=-69.424 Z=0
    g308: Circle CenterX=46.0728 CenterY=-87.7794 CenterZ=0 NormalX=0 NormalY=0 NormalZ=1 AngleXU=0 Radius=1
    g309: Circle CenterX=46.0728 CenterY=-91.7794 CenterZ=0 NormalX=0 NormalY=0 NormalZ=1 AngleXU=0 Radius=1
    g310: Circle CenterX=42.0728 CenterY=-91.7794 CenterZ=0 NormalX=0 NormalY=0 NormalZ=1 AngleXU=0 Radius=1
    g311: BSplineCurve PolesCount=3 KnotsCount=2 Degree=2 IsPeriodic=0
    g312: GeomPoint X=46.0728 Y=-87.7794 Z=0
    g313: GeomPoint X=42.0728 Y=-91.7794 Z=0
    g314: Circle CenterX=2.07281 CenterY=-91.7794 CenterZ=0 NormalX=0 NormalY=0 NormalZ=1 AngleXU=0 Radius=1
    g315: Circle CenterX=-1.92719 CenterY=-91.7794 CenterZ=0 NormalX=0 NormalY=0 NormalZ=1 AngleXU=0 Radius=1
    g316: Circle CenterX=1.57905 CenterY=-89.8542 CenterZ=0 NormalX=0 NormalY=0 NormalZ=1 AngleXU=0 Radius=1
    g317: BSplineCurve PolesCount=3 KnotsCount=2 Degree=2 IsPeriodic=0
    g318: GeomPoint X=2.07281 Y=-91.7794 Z=0
    g319: GeomPoint X=1.57905 Y=-89.8542 Z=0
    g320: LineSegment StartX=2.07281 StartY=-91.7794 StartZ=0 EndX=42.0728 EndY=-91.7794 EndZ=0
    g321: LineSegment StartX=46.0728 StartY=-87.7794 StartZ=0 EndX=46.0728 EndY=-69.424 EndZ=0
    g322: LineSegment StartX=42.5666 StartY=-67.3492 StartZ=0 EndX=1.57905 EndY=-89.8542 EndZ=0
    g323: Circle CenterX=322.073 CenterY=76.4095 CenterZ=0 NormalX=0 NormalY=0 NormalZ=1 AngleXU=0 Radius=4
    g324: BSplineCurve PolesCount=3 KnotsCount=2 Degree=2 IsPeriodic=0
    g325: GeomPoint X=318.073 Y=72.4095 Z=0
    g326: GeomPoint X=322.073 Y=76.4095 Z=0
    g327: Circle CenterX=375.073 CenterY=72.4095 CenterZ=0 NormalX=0 NormalY=0 NormalZ=1 AngleXU=0 Radius=1
    g328: Circle CenterX=375.073 CenterY=76.4095 CenterZ=0 NormalX=0 NormalY=0 NormalZ=1 AngleXU=0 Radius=1
    g329: Circle CenterX=371.073 CenterY=76.4095 CenterZ=0 NormalX=0 NormalY=0 NormalZ=1 AngleXU=0 Radius=1
    g330: BSplineCurve PolesCount=3 KnotsCount=2 Degree=2 IsPeriodic=0
    g331: GeomPoint X=375.073 Y=72.4095 Z=0
    g332: GeomPoint X=371.073 Y=76.4095 Z=0
    g333: LineSegment StartX=322.073 StartY=76.4095 StartZ=0 EndX=371.073 EndY=76.4095 EndZ=0
    g334: LineSegment StartX=318.073 StartY=72.4095 StartZ=0 EndX=318.073 EndY=-47.4805 EndZ=0
    g335: LineSegment StartX=375.073 StartY=72.4095 StartZ=0 EndX=375.073 EndY=-78.7896 EndZ=0
    g336: ArcOfCircle CenterX=-26.9272 CenterY=22.1087 CenterZ=0 NormalX=0 NormalY=0 NormalZ=1 AngleXU=0 Radius=4 StartAngle=5e-16 EndAngle=3.14159
    g337: LineSegment StartX=-22.9272 StartY=22.1087 StartZ=0 EndX=-18.9272 EndY=-83.7794 EndZ=0
    g338: LineSegment StartX=-34.9272 StartY=-83.7794 StartZ=0 EndX=-30.9272 EndY=22.1087 EndZ=0
    g339: ArcOfCircle CenterX=391.073 CenterY=22.1087 CenterZ=0 NormalX=0 NormalY=0 NormalZ=1 AngleXU=0 Radius=4 StartAngle=0 EndAngle=3.14159
    g340: LineSegment StartX=387.073 StartY=22.1087 StartZ=0 EndX=383.073 EndY=-83.7794 EndZ=0
    g341: LineSegment StartX=395.073 StartY=22.1087 StartZ=0 EndX=399.073 EndY=-83.7794 EndZ=0
    g342: Circle CenterX=-10.9272 CenterY=-78.7794 CenterZ=0 NormalX=0 NormalY=0 NormalZ=1 AngleXU=0 Radius=1
    g343: Circle CenterX=-10.9272 CenterY=-82.7794 CenterZ=0 NormalX=0 NormalY=0 NormalZ=1 AngleXU=0 Radius=1
    g344: Circle CenterX=-7.42095 CenterY=-80.8542 CenterZ=0 NormalX=0 NormalY=0 NormalZ=1 AngleXU=0 Radius=1
    g345: BSplineCurve PolesCount=3 KnotsCount=2 Degree=2 IsPeriodic=0
    g346: GeomPoint X=-10.9272 Y=-78.7794 Z=0
    g347: GeomPoint X=-7.42095 Y=-80.8542 Z=0
    g348: Circle CenterX=42.5666 CenterY=-53.4075 CenterZ=0 NormalX=0 NormalY=0 NormalZ=1 AngleXU=0 Radius=1
    g349: Circle CenterX=46.0728 CenterY=-51.4823 CenterZ=0 NormalX=0 NormalY=0 NormalZ=1 AngleXU=0 Radius=1
    g350: Circle CenterX=46.0728 CenterY=-47.4823 CenterZ=0 NormalX=0 NormalY=0 NormalZ=1 AngleXU=0 Radius=1
    g351: BSplineCurve PolesCount=3 KnotsCount=2 Degree=2 IsPeriodic=0
    g352: GeomPoint X=42.5666 Y=-53.4075 Z=0
    g353: GeomPoint X=46.0728 Y=-47.4823 Z=0
    g354: Circle CenterX=46.0728 CenterY=72.4095 CenterZ=0 NormalX=0 NormalY=0 NormalZ=1 AngleXU=0 Radius=1
    g355: Circle CenterX=46.0728 CenterY=76.4095 CenterZ=0 NormalX=0 NormalY=0 NormalZ=1 AngleXU=0 Radius=1
    g356: Circle CenterX=42.0728 CenterY=76.4095 CenterZ=0 NormalX=0 NormalY=0 NormalZ=1 AngleXU=0 Radius=1
    g357: BSplineCurve PolesCount=3 KnotsCount=2 Degree=2 IsPeriodic=0
    g358: GeomPoint X=46.0728 Y=72.4095 Z=0
    g359: GeomPoint X=42.0728 Y=76.4095 Z=0
    g360: Circle CenterX=-6.92718 CenterY=76.4095 CenterZ=0 NormalX=0 NormalY=0 NormalZ=1 AngleXU=0 Radius=1
    g361: Circle CenterX=-10.9272 CenterY=76.4095 CenterZ=0 NormalX=0 NormalY=0 NormalZ=1 AngleXU=0 Radius=1
    g362: Circle CenterX=-10.9272 CenterY=72.4095 CenterZ=0 NormalX=0 NormalY=0 NormalZ=1 AngleXU=0 Radius=1
    g363: BSplineCurve PolesCount=3 KnotsCount=2 Degree=2 IsPeriodic=0
    g364: GeomPoint X=-6.92718 Y=76.4095 Z=0
    g365: GeomPoint X=-10.9272 Y=72.4095 Z=0
    g366: LineSegment StartX=-10.9272 StartY=72.4095 StartZ=0 EndX=-10.9272 EndY=-78.7794 EndZ=0
    g367: LineSegment StartX=-7.42095 StartY=-80.8542 StartZ=0 EndX=42.5666 EndY=-53.4075 EndZ=0
    g368: LineSegment StartX=46.0728 StartY=-47.4823 StartZ=0 EndX=46.0728 EndY=72.4095 EndZ=0
    g369: LineSegment StartX=42.0728 StartY=76.4095 StartZ=0 EndX=-6.92719 EndY=76.4095 EndZ=0
    g370: LineSegment StartX=232.072 StartY=136.221 StartZ=0 EndX=232.072 EndY=-117.815 EndZ=0
    g371: LineSegment StartX=245.072 StartY=136.221 StartZ=0 EndX=245.072 EndY=-116.499 EndZ=0
    g372: LineSegment StartX=119.072 StartY=136.221 StartZ=0 EndX=119.072 EndY=-116.228 EndZ=0
    g373: LineSegment StartX=-42.9272 StartY=136.221 StartZ=0 EndX=407.073 EndY=136.221 EndZ=0
    g374: LineSegment StartX=232.072 StartY=136.221 StartZ=0 EndX=220.072 EndY=136.221 EndZ=0
    g375: LineSegment StartX=232.072 StartY=136.221 StartZ=0 EndX=232.072 EndY=124.221 EndZ=0
    g376: LineSegment StartX=220.072 StartY=136.221 StartZ=0 EndX=220.072 EndY=124.221 EndZ=0
    g377: LineSegment StartX=220.072 StartY=136.221 StartZ=0 EndX=226.072 EndY=136.221 EndZ=0
    g378: LineSegment StartX=220.072 StartY=136.221 StartZ=0 EndX=220.072 EndY=130.221 EndZ=0
    g379: LineSegment StartX=220.072 StartY=124.221 StartZ=0 EndX=226.072 EndY=124.221 EndZ=0
    g380: LineSegment StartX=232.072 StartY=124.221 StartZ=0 EndX=232.072 EndY=127.221 EndZ=0
    g381: LineSegment StartX=232.072 StartY=136.221 StartZ=0 EndX=232.072 EndY=133.221 EndZ=0
    g382-g386: Circle x5 (B-spline internal-alignment scaffolding for g387; pole/knot coordinates omitted)
    g387: BSplineCurve PolesCount=5 KnotsCount=3 Degree=3 IsPeriodic=0
    g388: GeomPoint X=232.072 Y=133.221 Z=0
    g389: GeomPoint X=223.072 Y=130.221 Z=0
    g390: GeomPoint X=232.072 Y=127.221 Z=0
    g391: LineSegment StartX=189.124 StartY=124.221 StartZ=0 EndX=302.073 EndY=124.221 EndZ=0
    g392: LineSegment StartX=132.072 StartY=136.221 StartZ=0 EndX=132.072 EndY=124.221 EndZ=0
    g393: LineSegment StartX=132.072 StartY=136.221 StartZ=0 EndX=144.072 EndY=136.221 EndZ=0
    g394: LineSegment StartX=144.072 StartY=136.221 StartZ=0 EndX=144.072 EndY=124.221 EndZ=0
    g395: LineSegment StartX=144.072 StartY=136.221 StartZ=0 EndX=138.072 EndY=136.221 EndZ=0
    g396: LineSegment StartX=144.072 StartY=136.221 StartZ=0 EndX=144.072 EndY=130.221 EndZ=0
    g397: LineSegment StartX=132.072 StartY=136.221 StartZ=0 EndX=132.072 EndY=133.221 EndZ=0
    g398: LineSegment StartX=132.072 StartY=133.221 StartZ=0 EndX=132.072 EndY=127.221 EndZ=0
    g399-g403: Circle x5 (B-spline internal-alignment scaffolding for g404; pole/knot coordinates omitted)
    g404: BSplineCurve PolesCount=5 KnotsCount=3 Degree=3 IsPeriodic=0
    g405: GeomPoint X=132.072 Y=133.221 Z=0
    g406: GeomPoint X=141.072 Y=130.221 Z=0
    g407: GeomPoint X=132.072 Y=127.221 Z=0
    ... +4 more geometry lines
  constraints (698):
    c: Vertical(g0)
    c: Vertical(g1)
    c: Block(g1)
    c: Block(g0)
    c: Weight(g4) = 1
    c: Equal(g4,g5)
    c: Equal(g4,g6)
    c: InternalAlignment(g4,g7)
    c: InternalAlignment(g5,g7)
    c: InternalAlignment(g6,g7)
    c: InternalAlignment(g8,g7)
    c: InternalAlignment(g9,g7)
    c: Weight(g10) = 1
    c: Equal(g10,g11)
    c: Equal(g10,g12)
    c: InternalAlignment(g10,g13)
    c: InternalAlignment(g11,g13)
    c: InternalAlignment(g12,g13)
    c: InternalAlignment(g14,g13)
    c: InternalAlignment(g15,g13)
    c: Block(g13)
    c: Block(g7)
    c: Weight(g16) = 1
    c: Equal(g16,g17)
    c: Equal(g16,g18)
    c: InternalAlignment(g16,g19)
    c: InternalAlignment(g17,g19)
    c: InternalAlignment(g18,g19)
    c: InternalAlignment(g20,g19)
    c: InternalAlignment(g21,g19)
    c: Weight(g22) = 1
    c: Equal(g22,g23)
    c: Equal(g22,g24)
    c: InternalAlignment(g22,g25)
    c: InternalAlignment(g23,g25)
    c: InternalAlignment(g24,g25)
    c: InternalAlignment(g26,g25)
    c: InternalAlignment(g27,g25)
    c: Block(g25)
    c: Block(g19)
    c: Weight(g28) = 1
    c: Equal(g28,g29)
    c: Equal(g28,g30)
    c: InternalAlignment(g28,g31)
    c: InternalAlignment(g29,g31)
    c: InternalAlignment(g30,g31)
    c: InternalAlignment(g32,g31)
    c: InternalAlignment(g33,g31)
    c: Weight(g34) = 1
    c: Equal(g34,g35)
    c: Equal(g34,g36)
    c: InternalAlignment(g34,g37)
    c: InternalAlignment(g35,g37)
    c: InternalAlignment(g36,g37)
    c: InternalAlignment(g38,g37)
    c: InternalAlignment(g39,g37)
    c: Block(g31)
    c: Block(g37)
    c: Coincident(g40,g1)
    c: Coincident(g40,g0)
    c: Horizontal(g40)
    c: Distance(g40) = 450
    c: Weight(g41) = 1
    c: Equal(g41,g42)
    c: Equal(g41,g43)
    c: InternalAlignment(g41,g44)
    c: InternalAlignment(g42,g44)
    c: InternalAlignment(g43,g44)
    c: InternalAlignment(g45,g44)
    c: InternalAlignment(g46,g44)
    c: Block(g44)
    c: Weight(g47) = 1
    c: Equal(g47,g48)
    c: Equal(g47,g49)
    c: InternalAlignment(g47,g50)
    c: InternalAlignment(g48,g50)
    c: InternalAlignment(g49,g50)
    c: InternalAlignment(g51,g50)
    c: InternalAlignment(g52,g50)
    c: Block(g50)
    c: Weight(g53) = 1
    c: Equal(g53,g54)
    c: Equal(g53,g55)
    c: InternalAlignment(g53,g56)
    c: InternalAlignment(g54,g56)
    c: InternalAlignment(g55,g56)
    c: InternalAlignment(g57,g56)
    c: InternalAlignment(g58,g56)
    c: Block(g56)
    c: Weight(g59) = 1
    c: Equal(g59,g60)
    c: Equal(g59,g61)
    c: InternalAlignment(g59,g62)
    c: InternalAlignment(g60,g62)
    c: InternalAlignment(g61,g62)
    c: InternalAlignment(g63,g62)
    c: InternalAlignment(g64,g62)
    c: Block(g62)
    c: Weight(g65) = 1
    c: Equal(g65,g66)
    c: Equal(g65,g67)
    c: InternalAlignment(g65,g68)
    c: InternalAlignment(g66,g68)
    c: InternalAlignment(g67,g68)
    c: InternalAlignment(g69,g68)
    c: InternalAlignment(g70,g68)
    c: Weight(g71) = 1
    c: Equal(g71,g72)
    c: Equal(g71,g73)
    c: InternalAlignment(g71,g74)
    c: InternalAlignment(g72,g74)
    c: InternalAlignment(g73,g74)
    c: InternalAlignment(g75,g74)
    c: InternalAlignment(g76,g74)
    c: Block(g68)
    c: Block(g74)
    c: Coincident(g77,g68)
    c: Coincident(g77,g74)
    c: Vertical(g77)
    c: Coincident(g78,g68)
    c: Coincident(g78,g50)
    c: Coincident(g79,g50)
    c: Coincident(g79,g74)
    c: Weight(g80) = 1
    c: Equal(g80,g81)
    c: Equal(g80,g82)
    c: InternalAlignment(g80,g83)
    c: InternalAlignment(g81,g83)
    c: InternalAlignment(g82,g83)
    c: InternalAlignment(g84,g83)
    c: InternalAlignment(g85,g83)
    c: Weight(g86) = 1
    c: Equal(g86,g87)
    c: Equal(g86,g88)
    c: InternalAlignment(g86,g89)
    c: InternalAlignment(g87,g89)
    c: InternalAlignment(g88,g89)
    c: InternalAlignment(g90,g89)
    c: InternalAlignment(g91,g89)
    c: Block(g83)
    c: Block(g89)
    c: Coincident(g92,g83)
    c: Coincident(g92,g89)
    c: Vertical(g92)
    c: Coincident(g93,g83)
    c: Coincident(g93,g44)
    c: Coincident(g94,g44)
    c: Coincident(g94,g89)
    c: Weight(g95) = 1
    c: Equal(g95,g96)
    c: Equal(g95,g97)
    c: InternalAlignment(g95,g98)
    c: InternalAlignment(g96,g98)
    c: InternalAlignment(g97,g98)
    c: InternalAlignment(g99,g98)
    c: InternalAlignment(g100,g98)
    c: Weight(g101) = 1
    c: Equal(g101,g102)
    c: Equal(g101,g103)
    c: InternalAlignment(g101,g104)
    c: InternalAlignment(g102,g104)
    c: InternalAlignment(g103,g104)
    c: InternalAlignment(g105,g104)
    c: InternalAlignment(g106,g104)
    c: Block(g98)
    c: Block(g104)
    c: Coincident(g107,g98)
    c: Coincident(g107,g104)
    c: Vertical(g107)
    c: Coincident(g108,g104)
    c: Coincident(g108,g62)
    c: Coincident(g109,g62)
    c: Coincident(g109,g98)
    c: Weight(g110) = 1
    c: Equal(g110,g111)
    c: Equal(g110,g112)
    c: InternalAlignment(g110,g113)
    c: InternalAlignment(g111,g113)
    c: InternalAlignment(g112,g113)
    c: InternalAlignment(g114,g113)
    c: InternalAlignment(g115,g113)
    c: Weight(g116) = 1
    c: Equal(g116,g117)
    c: Equal(g116,g118)
    c: InternalAlignment(g116,g119)
    c: InternalAlignment(g117,g119)
    c: InternalAlignment(g118,g119)
    c: InternalAlignment(g120,g119)
    c: InternalAlignment(g121,g119)
    c: Block(g113)
    c: Block(g119)
    c: Coincident(g122,g113)
    c: Coincident(g122,g119)
    c: Vertical(g122)
    c: Coincident(g123,g119)
    c: Coincident(g123,g56)
    c: Coincident(g124,g56)
    c: Coincident(g124,g113)
    c: Weight(g125) = 1
    c: Equal(g125,g126)
    c: Equal(g125,g127)
    c: InternalAlignment(g125,g128)
    c: InternalAlignment(g126,g128)
    c: InternalAlignment(g127,g128)
    c: InternalAlignment(g129,g128)
    c: InternalAlignment(g130,g128)
    c: Weight(g131) = 1
    c: Equal(g131,g132)
    c: Equal(g131,g133)
    c: InternalAlignment(g131,g134)
    c: InternalAlignment(g132,g134)
    c: InternalAlignment(g133,g134)
    c: InternalAlignment(g135,g134)
    c: InternalAlignment(g136,g134)
    c: Weight(g137) = 1
    c: Equal(g137,g138)
    c: Equal(g137,g139)
    c: InternalAlignment(g137,g140)
    c: InternalAlignment(g138,g140)
    c: InternalAlignment(g139,g140)
    c: InternalAlignment(g141,g140)
    c: InternalAlignment(g142,g140)
    c: Weight(g143) = 1
    c: Equal(g143,g144)
    c: Equal(g143,g145)
    c: InternalAlignment(g143,g146)
    c: InternalAlignment(g144,g146)
    c: InternalAlignment(g145,g146)
    c: InternalAlignment(g147,g146)
    c: InternalAlignment(g148,g146)
    c: Block(g146)
    c: Block(g140)
    c: Block(g134)
    c: Block(g128)
    c: Coincident(g149,g25)
    c: Coincident(g149,g146)
    c: Coincident(g150,g146)
    c: Coincident(g150,g140)
    c: Horizontal(g150)
    c: Coincident(g151,g140)
    c: Coincident(g151,g25)
    c: Vertical(g151)
    c: Coincident(g152,g19)
    c: Coincident(g152,g134)
    c: Vertical(g152)
    c: Coincident(g153,g134)
    c: Coincident(g153,g128)
    c: Horizontal(g153)
    c: Coincident(g154,g128)
    c: Coincident(g154,g19)
    c: Weight(g155) = 1
    c: Equal(g155,g156)
    c: Equal(g155,g157)
    c: InternalAlignment(g155,g158)
    c: InternalAlignment(g156,g158)
    c: InternalAlignment(g157,g158)
    c: InternalAlignment(g159,g158)
    c: InternalAlignment(g160,g158)
    c: Weight(g161) = 1
    c: Equal(g161,g162)
    c: Equal(g161,g163)
    c: InternalAlignment(g161,g164)
    c: InternalAlignment(g162,g164)
    c: InternalAlignment(g163,g164)
    c: InternalAlignment(g165,g164)
    c: InternalAlignment(g166,g164)
    c: Weight(g167) = 1
    c: Equal(g167,g168)
    c: Equal(g167,g169)
    c: InternalAlignment(g167,g170)
    c: InternalAlignment(g168,g170)
    c: InternalAlignment(g169,g170)
    c: InternalAlignment(g171,g170)
    c: InternalAlignment(g172,g170)
    c: Weight(g173) = 1
    c: Equal(g173,g174)
    c: Equal(g173,g175)
    c: InternalAlignment(g173,g176)
    c: InternalAlignment(g174,g176)
    c: InternalAlignment(g175,g176)
    c: InternalAlignment(g177,g176)
    c: InternalAlignment(g178,g176)
    c: Block(g176)
    c: Block(g170)
    c: Block(g164)
    c: Block(g158)
    c: Coincident(g179,g170)
    c: Coincident(g179,g7)
    c: Vertical(g179)
    c: Coincident(g180,g13)
    c: Coincident(g180,g164)
    c: Vertical(g180)
    c: Coincident(g181,g158)
    c: Coincident(g181,g13)
    c: Coincident(g182,g7)
    c: Weight(g183) = 1
    c: Equal(g183,g184)
    c: Equal(g183,g185)
    c: InternalAlignment(g183,g186)
    c: InternalAlignment(g184,g186)
    c: InternalAlignment(g185,g186)
    c: InternalAlignment(g187,g186)
    c: InternalAlignment(g188,g186)
    c: Weight(g189) = 1
    c: Equal(g189,g190)
    c: Equal(g189,g191)
    c: InternalAlignment(g189,g192)
    c: InternalAlignment(g190,g192)
    c: InternalAlignment(g191,g192)
    c: InternalAlignment(g193,g192)
    c: InternalAlignment(g194,g192)
    c: Block(g192)
    c: Block(g186)
    c: Coincident(g195,g192)
    c: Coincident(g195,g31)
    c: Coincident(g196,g31)
    c: Coincident(g196,g186)
    c: Coincident(g197,g186)
    c: Coincident(g197,g192)
    c: Vertical(g197)
    c: Weight(g198) = 1
    c: Equal(g198,g199)
    c: Equal(g198,g200)
    c: InternalAlignment(g198,g201)
    c: InternalAlignment(g199,g201)
    c: InternalAlignment(g200,g201)
    c: InternalAlignment(g202,g201)
    c: InternalAlignment(g203,g201)
    c: Weight(g204) = 1
    c: Equal(g204,g205)
    c: Equal(g204,g206)
    c: InternalAlignment(g204,g207)
    c: InternalAlignment(g205,g207)
    c: InternalAlignment(g206,g207)
    c: InternalAlignment(g208,g207)
    c: InternalAlignment(g209,g207)
    c: Block(g207)
    c: Block(g201)
    c: Coincident(g210,g201)
    c: Coincident(g210,g37)
    c: Coincident(g211,g37)
    c: Coincident(g211,g207)
    c: Coincident(g212,g207)
    c: Coincident(g212,g201)
    c: Vertical(g212)
    c: Horizontal(g213)
    c: Block(g213)
    c: Vertical(g214)
    c: Block(g214)
    c: Block(g215)
    c: Weight(g216) = 1
    c: Equal(g216,g217)
    c: Equal(g216,g218)
    c: InternalAlignment(g216,g219)
    c: InternalAlignment(g217,g219)
    c: InternalAlignment(g218,g219)
    c: InternalAlignment(g220,g219)
    c: InternalAlignment(g221,g219)
    c: Weight(g222) = 1
    c: Equal(g222,g223)
    c: Equal(g222,g224)
    c: InternalAlignment(g222,g225)
    c: InternalAlignment(g223,g225)
    c: InternalAlignment(g224,g225)
    c: InternalAlignment(g226,g225)
    c: InternalAlignment(g227,g225)
    c: Weight(g228) = 1
    c: Equal(g228,g229)
    c: Equal(g228,g230)
    c: InternalAlignment(g228,g231)
    c: InternalAlignment(g229,g231)
    c: InternalAlignment(g230,g231)
    c: InternalAlignment(g232,g231)
    c: InternalAlignment(g233,g231)
    c: Weight(g234) = 1
    c: Equal(g234,g235)
    c: Equal(g234,g236)
    c: InternalAlignment(g234,g237)
    c: InternalAlignment(g235,g237)
    c: InternalAlignment(g236,g237)
    c: InternalAlignment(g238,g237)
    c: InternalAlignment(g239,g237)
    c: Block(g219)
    c: Block(g225)
    c: Block(g231)
    c: Block(g237)
    c: Coincident(g240,g225)
    c: Coincident(g240,g219)
    c: Horizontal(g240)
    c: Block(g182)
    c: Weight(g241) = 1
    c: Equal(g241,g242)
    c: Equal(g241,g243)
    c: InternalAlignment(g241,g244)
    c: InternalAlignment(g242,g244)
    c: InternalAlignment(g243,g244)
    c: InternalAlignment(g245,g244)
    c: InternalAlignment(g246,g244)
    c: Weight(g247) = 1
    c: Equal(g247,g248)
    c: Equal(g247,g249)
    c: InternalAlignment(g247,g250)
    c: InternalAlignment(g248,g250)
    c: InternalAlignment(g249,g250)
    c: InternalAlignment(g251,g250)
    c: InternalAlignment(g252,g250)
    c: Block(g244)
    c: Block(g250)
    c: Coincident(g253,g244)
    c: Coincident(g253,g250)
    c: Weight(g254) = 1
    c: Equal(g254,g255)
    c: Equal(g254,g256)
    c: InternalAlignment(g254,g257)
    c: InternalAlignment(g255,g257)
    c: InternalAlignment(g256,g257)
    c: InternalAlignment(g258,g257)
    c: InternalAlignment(g259,g257)
    c: Weight(g260) = 1
    c: Equal(g260,g261)
    c: Equal(g260,g262)
    c: InternalAlignment(g260,g263)
    c: InternalAlignment(g261,g263)
    c: InternalAlignment(g262,g263)
    c: InternalAlignment(g264,g263)
    c: InternalAlignment(g265,g263)
    c: Weight(g266) = 1
    c: Equal(g266,g267)
    c: Equal(g266,g268)
    c: InternalAlignment(g266,g269)
    c: InternalAlignment(g267,g269)
    c: InternalAlignment(g268,g269)
    c: InternalAlignment(g270,g269)
    c: InternalAlignment(g271,g269)
    c: Block(g269)
    c: Block(g263)
    c: Block(g257)
    c: Coincident(g272,g263)
    c: Coincident(g272,g257)
    c: Coincident(g273,g257)
    c: Coincident(g273,g269)
    c: Vertical(g273)
    c: Coincident(g274,g269)
    c: Coincident(g274,g263)
    c: Horizontal(g274)
    c: Weight(g275) = 1
    c: Equal(g275,g276)
    c: InternalAlignment(g275,g277)
    c: InternalAlignment(g276,g277)
    c: InternalAlignment(g278,g277)
    c: InternalAlignment(g279,g277)
    c: Weight(g280) = 1
    c: InternalAlignment(g281,g283)
    c: InternalAlignment(g282,g283)
    c: InternalAlignment(g284,g283)
    c: InternalAlignment(g285,g283)
    c: Weight(g286) = 1
    c: Equal(g286,g287)
    c: Equal(g286,g288)
    c: InternalAlignment(g286,g289)
    c: InternalAlignment(g287,g289)
    c: InternalAlignment(g288,g289)
    c: InternalAlignment(g290,g289)
    c: InternalAlignment(g291,g289)
    c: Equal(g292,g293)
    c: Equal(g292,g294)
    c: InternalAlignment(g292,g295)
    c: InternalAlignment(g293,g295)
    c: InternalAlignment(g294,g295)
    c: InternalAlignment(g296,g295)
    c: InternalAlignment(g297,g295)
    c: Block(g283)
    c: Block(g289)
    c: Block(g295)
    c: Block(g277)
    c: Coincident(g298,g277)
    c: Coincident(g298,g283)
    c: Horizontal(g298)
    c: Coincident(g299,g283)
    c: Coincident(g299,g289)
    c: Vertical(g299)
    c: Coincident(g300,g289)
    c: Coincident(g300,g295)
    c: Horizontal(g300)
    c: Coincident(g301,g295)
    c: Coincident(g301,g277)
    c: Weight(g302) = 1
    c: Equal(g302,g303)
    c: Equal(g302,g304)
    c: InternalAlignment(g302,g305)
    c: InternalAlignment(g303,g305)
    c: InternalAlignment(g304,g305)
    c: InternalAlignment(g306,g305)
    c: InternalAlignment(g307,g305)
    c: Weight(g308) = 1
    c: Equal(g308,g309)
    c: Equal(g308,g310)
    c: InternalAlignment(g308,g311)
    c: InternalAlignment(g309,g311)
    c: InternalAlignment(g310,g311)
    c: InternalAlignment(g312,g311)
    c: Weight(g314) = 1
    c: Equal(g314,g315)
    c: Equal(g314,g316)
    c: InternalAlignment(g314,g317)
    c: InternalAlignment(g315,g317)
    c: InternalAlignment(g316,g317)
    c: InternalAlignment(g318,g317)
    c: InternalAlignment(g319,g317)
    c: Block(g317)
    c: Block(g311)
    c: Block(g305)
    c: Coincident(g320,g317)
    c: Coincident(g320,g311)
    c: Horizontal(g320)
    c: Coincident(g321,g311)
    c: Coincident(g321,g305)
    c: Vertical(g321)
    c: Coincident(g322,g305)
    c: Coincident(g322,g317)
    c: InternalAlignment(g323,g324)
    c: InternalAlignment(g325,g324)
    c: InternalAlignment(g326,g324)
    c: Block(g324)
    c: Equal(g327,g328)
    c: Equal(g327,g329)
    c: InternalAlignment(g327,g330)
    c: InternalAlignment(g328,g330)
    c: InternalAlignment(g329,g330)
    c: InternalAlignment(g331,g330)
    c: InternalAlignment(g332,g330)
    c: Block(g330)
    c: Coincident(g333,g324)
    c: Horizontal(g333)
    c: Block(g333)
    c: Coincident(g334,g324)
    c: Coincident(g334,g250)
    c: Vertical(g334)
    c: Coincident(g335,g330)
    c: Coincident(g335,g244)
    c: Vertical(g335)
    c: Block(g336)
    c: Block(g2)
    c: Distance(g334) = 119.89
    c: Coincident(g337,g336)
    c: Coincident(g337,g2)
    c: Coincident(g338,g2)
    c: Coincident(g338,g336)
    c: Block(g3)
    c: Block(g339)
    c: Coincident(g340,g339)
    c: Coincident(g340,g3)
    c: Coincident(g341,g339)
    c: Coincident(g341,g3)
    c: Block(g341)
    c: Block(g340)
    c: Weight(g342) = 1
    c: Equal(g342,g343)
    c: Equal(g342,g344)
    c: InternalAlignment(g342,g345)
    c: InternalAlignment(g343,g345)
    c: InternalAlignment(g344,g345)
    c: InternalAlignment(g346,g345)
    c: InternalAlignment(g347,g345)
    c: Weight(g348) = 1
    c: Equal(g348,g349)
    c: Equal(g348,g350)
    c: InternalAlignment(g348,g351)
    c: InternalAlignment(g349,g351)
    c: InternalAlignment(g350,g351)
    c: InternalAlignment(g352,g351)
    c: InternalAlignment(g353,g351)
    c: Weight(g354) = 1
    c: Equal(g354,g355)
    c: Equal(g354,g356)
    c: InternalAlignment(g354,g357)
    c: InternalAlignment(g355,g357)
    c: InternalAlignment(g356,g357)
    c: InternalAlignment(g358,g357)
    c: InternalAlignment(g359,g357)
    c: Weight(g360) = 1
    c: Equal(g360,g361)
    c: Equal(g360,g362)
    c: InternalAlignment(g360,g363)
    c: InternalAlignment(g361,g363)
    c: InternalAlignment(g362,g363)
    c: InternalAlignment(g364,g363)
    c: InternalAlignment(g365,g363)
    c: Block(g363)
    c: Block(g357)
    c: Block(g351)
    c: Block(g345)
    c: Coincident(g366,g363)
    c: Coincident(g366,g345)
    c: Vertical(g366)
    c: Coincident(g367,g345)
    c: Coincident(g367,g351)
    c: Coincident(g368,g351)
    c: Coincident(g368,g357)
    c: Vertical(g368)
    c: Coincident(g369,g357)
    c: Coincident(g369,g363)
    c: Horizontal(g369)
    c: Vertical(g370)
    c: Vertical(g371)
    c: Vertical(g372)
    c: Coincident(g373,g0)
    c: Coincident(g373,g1)
    c: Horizontal(g373)
    c: Block(g373)
    c: Distance(g373) = 450
    c: Block(g371)
    c: Block(g370)
    c: Block(g372)
    c: Distance(g0) = 240
    c: Horizontal(g374)
    c: Distance(g374) = 12
    c: Coincident(g374,g370)
    c: Vertical(g375)
    c: Distance(g375) = 12
    c: Coincident(g375,g370)
    c: Coincident(g376,g374)
    c: Vertical(g376)
    c: Horizontal(g377)
    c: Vertical(g378)
    c: Distance(g378) = 6
    c: Coincident(g378,g374)
    c: Coincident(g377,g374)
    c: Block(g376)
    c: Coincident(g379,g376)
    c: Horizontal(g379)
    c: Distance(g379) = 6
    c: Vertical(g380)
    c: Distance(g380) = 3
    c: Vertical(g381)
    c: Distance(g381) = 3
    c: Coincident(g381,g370)
    c: Coincident(g375,g380)
    c: Coincident(g387,g381)
    c: Weight(g382) = 1
    c: Equal(g382,g383)
    c: Coincident(g383,g377)
    c: Equal(g382,g384)
    c: Coincident(g384,g378)
    c: Equal(g382,g385)
    c: Coincident(g385,g379)
    c: Equal(g382,g386)
    c: Coincident(g387,g380)
    c: InternalAlignment(g382-g386 -> g387) x5
    c: InternalAlignment(g388,g387)
    c: InternalAlignment(g389,g387)
    c: InternalAlignment(g390,g387)
    c: Coincident(g391,g164)
    c: Coincident(g391,g158)
    c: Horizontal(g391)
    c: Block(g387)
    c: Vertical(g392)
    c: Distance(g392) = 12
    c: Horizontal(g393)
    c: Distance(g393) = 12
    c: Coincident(g394,g393)
    c: Vertical(g394)
    c: Distance(g394) = 12
    c: Horizontal(g395)
    c: Distance(g395) = 6
    c: Coincident(g395,g393)
    c: Vertical(g396)
    c: Distance(g396) = 6
    c: Coincident(g396,g393)
    c: Vertical(g397)
    c: Distance(g397) = 3
    c: Vertical(g398)
    c: Distance(g398) = 6
    c: Coincident(g398,g397)
    c: Coincident(g404,g397)
    c: Weight(g399) = 1
    c: Equal(g399,g400)
    c: Coincident(g400,g395)
    c: Equal(g399,g401)
    c: Coincident(g401,g396)
    c: Equal(g399,g402)
    c: Equal(g399,g403)
    c: Coincident(g404,g398)
    c: InternalAlignment(g399-g403 -> g404) x5
    c: InternalAlignment(g405,g404)
    c: InternalAlignment(g406,g404)
    c: InternalAlignment(g407,g404)
    c: Coincident(g408,g392)
    c: Coincident(g408,g170)
    c: Horizontal(g408)
    c: Block(g404)
    c: Coincident(g409,g176)
    c: Coincident(g409,g392)
    c: Horizontal(g409)
    c: Block(g408)
    c: Coincident(g411,g392)
    c: PointOnObject(g411,g153)
    c: Vertical(g411)
FEATURE [Part::Extrusion] Extrude005
  Base = -> Sketch003
  Dir = (0,0,1)
  DirMode = 2
  FaceMakerClass = Part::FaceMakerBullseye
  LengthFwd = 24
  LengthRev = 0
  Solid = true
  Symmetric = false
